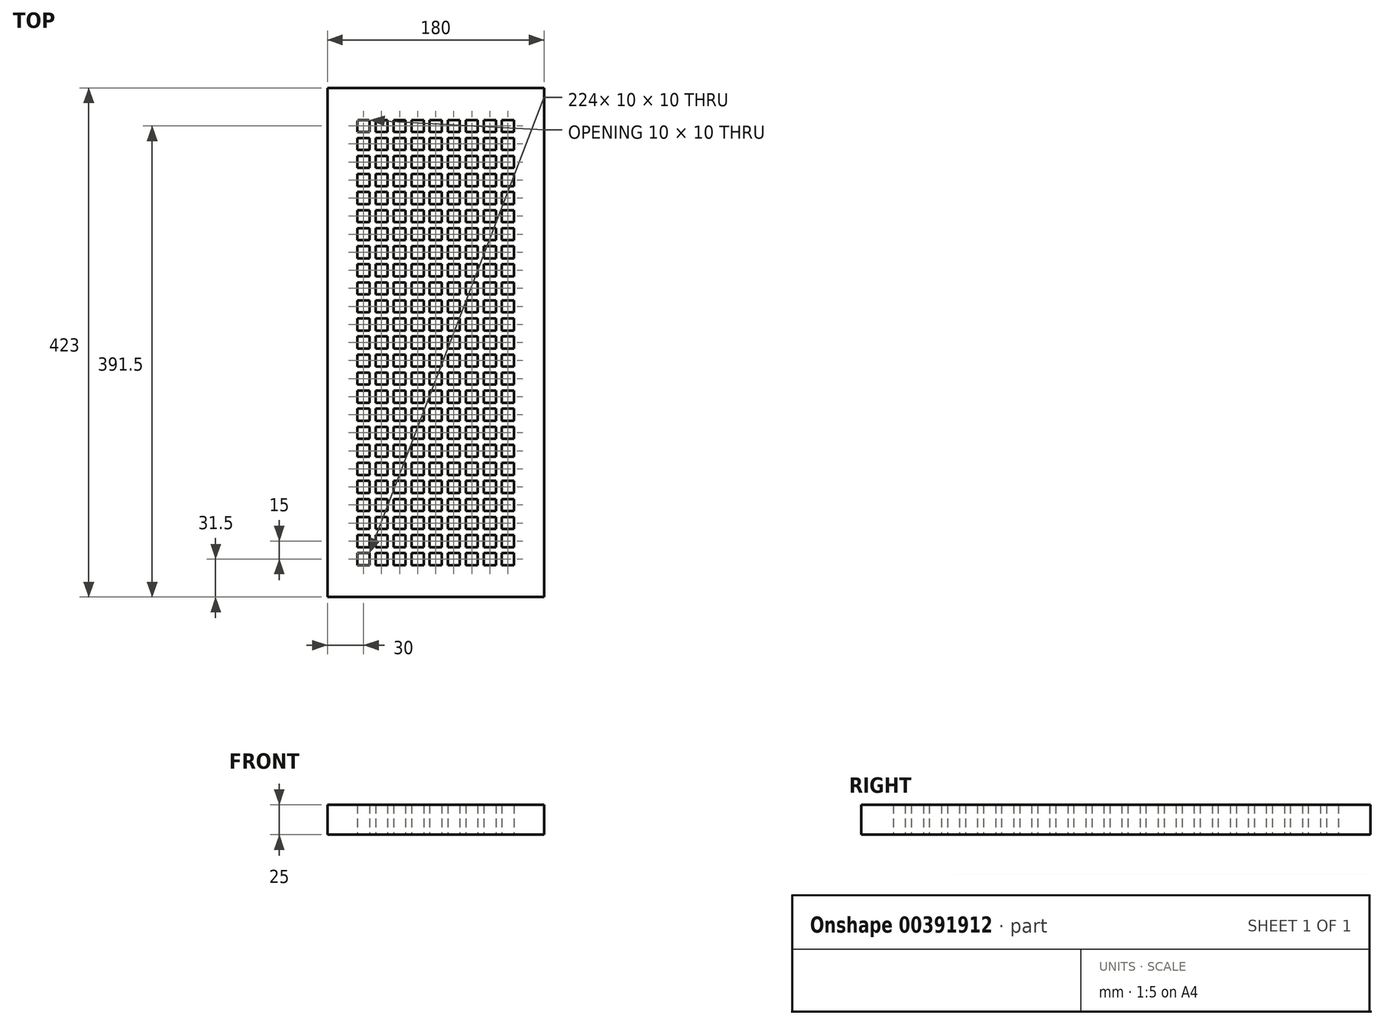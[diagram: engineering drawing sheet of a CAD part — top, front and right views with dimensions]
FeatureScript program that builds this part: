
annotation { "Feature Type Name" : "Feature", "Feature Type Description" : "" }
export const myFeature = defineFeature(function(context is Context, id is Id, definition is map)
    precondition{}
    {
        {
            var Q0;
            Q0=qCreatedBy(makeId("Top.planeOp"),FACE);
            var sketch = newSketch(context, id + "F0", { "sketchPlane" : qUnion([Q0])});
            skLineSegment(sketch, "E0.bottom", {"start": v(-180, 423) * mm, "end": v(0, 423) * mm});
            skLineSegment(sketch, "E0.top", {"start": v(-180, 0) * mm, "end": v(0, 0) * mm});
            skLineSegment(sketch, "E0.left", {"start": v(-180, 423) * mm, "end": v(-180, 0) * mm});
            skLineSegment(sketch, "E0.right", {"start": v(0, 423) * mm, "end": v(0, 0) * mm});
            skLineSegment(sketch, "E1", {"start": v(-153.5, 396.5) * mm, "end": v(-146.5, 396.5) * mm});
            skLineSegment(sketch, "E2", {"start": v(-155, 386.5) * mm, "end": v(-145, 386.5) * mm});
            skLineSegment(sketch, "E3", {"start": v(-145, 386.5) * mm, "end": v(-145, 395) * mm});
            skLineSegment(sketch, "E4.trimOffspring", {"start": v(-155, 386.5) * mm, "end": v(-155, 395) * mm});
            skLineSegment(sketch, "E5.0.1.0", {"start": v(-155, 371.5) * mm, "end": v(-155, 381.5) * mm});
            skLineSegment(sketch, "E5.0.1.1", {"start": v(-145, 371.5) * mm, "end": v(-145, 381.5) * mm});
            skLineSegment(sketch, "E5.0.1.2", {"start": v(-155, 371.5) * mm, "end": v(-145, 371.5) * mm});
            skLineSegment(sketch, "E5.0.1.3", {"start": v(-155, 381.5) * mm, "end": v(-145, 381.5) * mm});
            skLineSegment(sketch, "E5.0.2.0", {"start": v(-155, 356.5) * mm, "end": v(-155, 366.5) * mm});
            skLineSegment(sketch, "E5.0.2.1", {"start": v(-145, 356.5) * mm, "end": v(-145, 366.5) * mm});
            skLineSegment(sketch, "E5.0.2.2", {"start": v(-155, 356.5) * mm, "end": v(-145, 356.5) * mm});
            skLineSegment(sketch, "E5.0.2.3", {"start": v(-155, 366.5) * mm, "end": v(-145, 366.5) * mm});
            skLineSegment(sketch, "E5.0.3.0", {"start": v(-155, 341.5) * mm, "end": v(-155, 351.5) * mm});
            skLineSegment(sketch, "E5.0.3.1", {"start": v(-145, 341.5) * mm, "end": v(-145, 351.5) * mm});
            skLineSegment(sketch, "E5.0.3.2", {"start": v(-155, 341.5) * mm, "end": v(-145, 341.5) * mm});
            skLineSegment(sketch, "E5.0.3.3", {"start": v(-155, 351.5) * mm, "end": v(-145, 351.5) * mm});
            skLineSegment(sketch, "E5.0.4.0", {"start": v(-155, 326.5) * mm, "end": v(-155, 336.5) * mm});
            skLineSegment(sketch, "E5.0.4.1", {"start": v(-145, 326.5) * mm, "end": v(-145, 336.5) * mm});
            skLineSegment(sketch, "E5.0.4.2", {"start": v(-155, 326.5) * mm, "end": v(-145, 326.5) * mm});
            skLineSegment(sketch, "E5.0.4.3", {"start": v(-155, 336.5) * mm, "end": v(-145, 336.5) * mm});
            skLineSegment(sketch, "E5.0.5.0", {"start": v(-155, 311.5) * mm, "end": v(-155, 321.5) * mm});
            skLineSegment(sketch, "E5.0.5.1", {"start": v(-145, 311.5) * mm, "end": v(-145, 321.5) * mm});
            skLineSegment(sketch, "E5.0.5.2", {"start": v(-155, 311.5) * mm, "end": v(-145, 311.5) * mm});
            skLineSegment(sketch, "E5.0.5.3", {"start": v(-155, 321.5) * mm, "end": v(-145, 321.5) * mm});
            skLineSegment(sketch, "E5.0.6.0", {"start": v(-155, 296.5) * mm, "end": v(-155, 306.5) * mm});
            skLineSegment(sketch, "E5.0.6.1", {"start": v(-145, 296.5) * mm, "end": v(-145, 306.5) * mm});
            skLineSegment(sketch, "E5.0.6.2", {"start": v(-155, 296.5) * mm, "end": v(-145, 296.5) * mm});
            skLineSegment(sketch, "E5.0.6.3", {"start": v(-155, 306.5) * mm, "end": v(-145, 306.5) * mm});
            skLineSegment(sketch, "E5.0.7.0", {"start": v(-155, 281.5) * mm, "end": v(-155, 291.5) * mm});
            skLineSegment(sketch, "E5.0.7.1", {"start": v(-145, 281.5) * mm, "end": v(-145, 291.5) * mm});
            skLineSegment(sketch, "E5.0.7.2", {"start": v(-155, 281.5) * mm, "end": v(-145, 281.5) * mm});
            skLineSegment(sketch, "E5.0.7.3", {"start": v(-155, 291.5) * mm, "end": v(-145, 291.5) * mm});
            skLineSegment(sketch, "E5.0.8.0", {"start": v(-155, 266.5) * mm, "end": v(-155, 276.5) * mm});
            skLineSegment(sketch, "E5.0.8.1", {"start": v(-145, 266.5) * mm, "end": v(-145, 276.5) * mm});
            skLineSegment(sketch, "E5.0.8.2", {"start": v(-155, 266.5) * mm, "end": v(-145, 266.5) * mm});
            skLineSegment(sketch, "E5.0.8.3", {"start": v(-155, 276.5) * mm, "end": v(-145, 276.5) * mm});
            skLineSegment(sketch, "E5.0.9.0", {"start": v(-155, 251.5) * mm, "end": v(-155, 261.5) * mm});
            skLineSegment(sketch, "E5.0.9.1", {"start": v(-145, 251.5) * mm, "end": v(-145, 261.5) * mm});
            skLineSegment(sketch, "E5.0.9.2", {"start": v(-155, 251.5) * mm, "end": v(-145, 251.5) * mm});
            skLineSegment(sketch, "E5.0.9.3", {"start": v(-155, 261.5) * mm, "end": v(-145, 261.5) * mm});
            skLineSegment(sketch, "E5.0.10.0", {"start": v(-155, 236.5) * mm, "end": v(-155, 246.5) * mm});
            skLineSegment(sketch, "E5.0.10.1", {"start": v(-145, 236.5) * mm, "end": v(-145, 246.5) * mm});
            skLineSegment(sketch, "E5.0.10.2", {"start": v(-155, 236.5) * mm, "end": v(-145, 236.5) * mm});
            skLineSegment(sketch, "E5.0.10.3", {"start": v(-155, 246.5) * mm, "end": v(-145, 246.5) * mm});
            skLineSegment(sketch, "E5.0.11.0", {"start": v(-155, 221.5) * mm, "end": v(-155, 231.5) * mm});
            skLineSegment(sketch, "E5.0.11.1", {"start": v(-145, 221.5) * mm, "end": v(-145, 231.5) * mm});
            skLineSegment(sketch, "E5.0.11.2", {"start": v(-155, 221.5) * mm, "end": v(-145, 221.5) * mm});
            skLineSegment(sketch, "E5.0.11.3", {"start": v(-155, 231.5) * mm, "end": v(-145, 231.5) * mm});
            skLineSegment(sketch, "E5.0.12.0", {"start": v(-155, 206.5) * mm, "end": v(-155, 216.5) * mm});
            skLineSegment(sketch, "E5.0.12.1", {"start": v(-145, 206.5) * mm, "end": v(-145, 216.5) * mm});
            skLineSegment(sketch, "E5.0.12.2", {"start": v(-155, 206.5) * mm, "end": v(-145, 206.5) * mm});
            skLineSegment(sketch, "E5.0.12.3", {"start": v(-155, 216.5) * mm, "end": v(-145, 216.5) * mm});
            skLineSegment(sketch, "E5.0.13.0", {"start": v(-155, 191.5) * mm, "end": v(-155, 201.5) * mm});
            skLineSegment(sketch, "E5.0.13.1", {"start": v(-145, 191.5) * mm, "end": v(-145, 201.5) * mm});
            skLineSegment(sketch, "E5.0.13.2", {"start": v(-155, 191.5) * mm, "end": v(-145, 191.5) * mm});
            skLineSegment(sketch, "E5.0.13.3", {"start": v(-155, 201.5) * mm, "end": v(-145, 201.5) * mm});
            skLineSegment(sketch, "E5.0.14.0", {"start": v(-155, 176.5) * mm, "end": v(-155, 186.5) * mm});
            skLineSegment(sketch, "E5.0.14.1", {"start": v(-145, 176.5) * mm, "end": v(-145, 186.5) * mm});
            skLineSegment(sketch, "E5.0.14.2", {"start": v(-155, 176.5) * mm, "end": v(-145, 176.5) * mm});
            skLineSegment(sketch, "E5.0.14.3", {"start": v(-155, 186.5) * mm, "end": v(-145, 186.5) * mm});
            skLineSegment(sketch, "E5.0.15.0", {"start": v(-155, 161.5) * mm, "end": v(-155, 171.5) * mm});
            skLineSegment(sketch, "E5.0.15.1", {"start": v(-145, 161.5) * mm, "end": v(-145, 171.5) * mm});
            skLineSegment(sketch, "E5.0.15.2", {"start": v(-155, 161.5) * mm, "end": v(-145, 161.5) * mm});
            skLineSegment(sketch, "E5.0.15.3", {"start": v(-155, 171.5) * mm, "end": v(-145, 171.5) * mm});
            skLineSegment(sketch, "E5.0.16.0", {"start": v(-155, 146.5) * mm, "end": v(-155, 156.5) * mm});
            skLineSegment(sketch, "E5.0.16.1", {"start": v(-145, 146.5) * mm, "end": v(-145, 156.5) * mm});
            skLineSegment(sketch, "E5.0.16.2", {"start": v(-155, 146.5) * mm, "end": v(-145, 146.5) * mm});
            skLineSegment(sketch, "E5.0.16.3", {"start": v(-155, 156.5) * mm, "end": v(-145, 156.5) * mm});
            skLineSegment(sketch, "E5.0.17.0", {"start": v(-155, 131.5) * mm, "end": v(-155, 141.5) * mm});
            skLineSegment(sketch, "E5.0.17.1", {"start": v(-145, 131.5) * mm, "end": v(-145, 141.5) * mm});
            skLineSegment(sketch, "E5.0.17.2", {"start": v(-155, 131.5) * mm, "end": v(-145, 131.5) * mm});
            skLineSegment(sketch, "E5.0.17.3", {"start": v(-155, 141.5) * mm, "end": v(-145, 141.5) * mm});
            skLineSegment(sketch, "E5.0.18.0", {"start": v(-155, 116.5) * mm, "end": v(-155, 126.5) * mm});
            skLineSegment(sketch, "E5.0.18.1", {"start": v(-145, 116.5) * mm, "end": v(-145, 126.5) * mm});
            skLineSegment(sketch, "E5.0.18.2", {"start": v(-155, 116.5) * mm, "end": v(-145, 116.5) * mm});
            skLineSegment(sketch, "E5.0.18.3", {"start": v(-155, 126.5) * mm, "end": v(-145, 126.5) * mm});
            skLineSegment(sketch, "E5.0.19.0", {"start": v(-155, 101.5) * mm, "end": v(-155, 111.5) * mm});
            skLineSegment(sketch, "E5.0.19.1", {"start": v(-145, 101.5) * mm, "end": v(-145, 111.5) * mm});
            skLineSegment(sketch, "E5.0.19.2", {"start": v(-155, 101.5) * mm, "end": v(-145, 101.5) * mm});
            skLineSegment(sketch, "E5.0.19.3", {"start": v(-155, 111.5) * mm, "end": v(-145, 111.5) * mm});
            skLineSegment(sketch, "E5.0.20.0", {"start": v(-155, 86.5) * mm, "end": v(-155, 96.5) * mm});
            skLineSegment(sketch, "E5.0.20.1", {"start": v(-145, 86.5) * mm, "end": v(-145, 96.5) * mm});
            skLineSegment(sketch, "E5.0.20.2", {"start": v(-155, 86.5) * mm, "end": v(-145, 86.5) * mm});
            skLineSegment(sketch, "E5.0.20.3", {"start": v(-155, 96.5) * mm, "end": v(-145, 96.5) * mm});
            skLineSegment(sketch, "E5.0.21.0", {"start": v(-155, 71.5) * mm, "end": v(-155, 81.5) * mm});
            skLineSegment(sketch, "E5.0.21.1", {"start": v(-145, 71.5) * mm, "end": v(-145, 81.5) * mm});
            skLineSegment(sketch, "E5.0.21.2", {"start": v(-155, 71.5) * mm, "end": v(-145, 71.5) * mm});
            skLineSegment(sketch, "E5.0.21.3", {"start": v(-155, 81.5) * mm, "end": v(-145, 81.5) * mm});
            skLineSegment(sketch, "E5.0.22.0", {"start": v(-155, 56.5) * mm, "end": v(-155, 66.5) * mm});
            skLineSegment(sketch, "E5.0.22.1", {"start": v(-145, 56.5) * mm, "end": v(-145, 66.5) * mm});
            skLineSegment(sketch, "E5.0.22.2", {"start": v(-155, 56.5) * mm, "end": v(-145, 56.5) * mm});
            skLineSegment(sketch, "E5.0.22.3", {"start": v(-155, 66.5) * mm, "end": v(-145, 66.5) * mm});
            skLineSegment(sketch, "E5.0.23.0", {"start": v(-155, 41.5) * mm, "end": v(-155, 51.5) * mm});
            skLineSegment(sketch, "E5.0.23.1", {"start": v(-145, 41.5) * mm, "end": v(-145, 51.5) * mm});
            skLineSegment(sketch, "E5.0.23.2", {"start": v(-155, 41.5) * mm, "end": v(-145, 41.5) * mm});
            skLineSegment(sketch, "E5.0.23.3", {"start": v(-155, 51.5) * mm, "end": v(-145, 51.5) * mm});
            skLineSegment(sketch, "E5.0.24.0", {"start": v(-155, 26.5) * mm, "end": v(-155, 36.5) * mm});
            skLineSegment(sketch, "E5.0.24.1", {"start": v(-145, 26.5) * mm, "end": v(-145, 36.5) * mm});
            skLineSegment(sketch, "E5.0.24.2", {"start": v(-155, 26.5) * mm, "end": v(-145, 26.5) * mm});
            skLineSegment(sketch, "E5.0.24.3", {"start": v(-155, 36.5) * mm, "end": v(-145, 36.5) * mm});
            skLineSegment(sketch, "E5.1.0.0", {"start": v(-140, 386.5) * mm, "end": v(-140, 396.5) * mm});
            skLineSegment(sketch, "E5.1.0.1", {"start": v(-130, 386.5) * mm, "end": v(-130, 396.5) * mm});
            skLineSegment(sketch, "E5.1.0.2", {"start": v(-140, 386.5) * mm, "end": v(-130, 386.5) * mm});
            skLineSegment(sketch, "E5.1.0.3", {"start": v(-140, 396.5) * mm, "end": v(-130, 396.5) * mm});
            skLineSegment(sketch, "E5.1.1.0", {"start": v(-140, 371.5) * mm, "end": v(-140, 381.5) * mm});
            skLineSegment(sketch, "E5.1.1.1", {"start": v(-130, 371.5) * mm, "end": v(-130, 381.5) * mm});
            skLineSegment(sketch, "E5.1.1.2", {"start": v(-140, 371.5) * mm, "end": v(-130, 371.5) * mm});
            skLineSegment(sketch, "E5.1.1.3", {"start": v(-140, 381.5) * mm, "end": v(-130, 381.5) * mm});
            skLineSegment(sketch, "E5.1.2.0", {"start": v(-140, 356.5) * mm, "end": v(-140, 366.5) * mm});
            skLineSegment(sketch, "E5.1.2.1", {"start": v(-130, 356.5) * mm, "end": v(-130, 366.5) * mm});
            skLineSegment(sketch, "E5.1.2.2", {"start": v(-140, 356.5) * mm, "end": v(-130, 356.5) * mm});
            skLineSegment(sketch, "E5.1.2.3", {"start": v(-140, 366.5) * mm, "end": v(-130, 366.5) * mm});
            skLineSegment(sketch, "E5.1.3.0", {"start": v(-140, 341.5) * mm, "end": v(-140, 351.5) * mm});
            skLineSegment(sketch, "E5.1.3.1", {"start": v(-130, 341.5) * mm, "end": v(-130, 351.5) * mm});
            skLineSegment(sketch, "E5.1.3.2", {"start": v(-140, 341.5) * mm, "end": v(-130, 341.5) * mm});
            skLineSegment(sketch, "E5.1.3.3", {"start": v(-140, 351.5) * mm, "end": v(-130, 351.5) * mm});
            skLineSegment(sketch, "E5.1.4.0", {"start": v(-140, 326.5) * mm, "end": v(-140, 336.5) * mm});
            skLineSegment(sketch, "E5.1.4.1", {"start": v(-130, 326.5) * mm, "end": v(-130, 336.5) * mm});
            skLineSegment(sketch, "E5.1.4.2", {"start": v(-140, 326.5) * mm, "end": v(-130, 326.5) * mm});
            skLineSegment(sketch, "E5.1.4.3", {"start": v(-140, 336.5) * mm, "end": v(-130, 336.5) * mm});
            skLineSegment(sketch, "E5.1.5.0", {"start": v(-140, 311.5) * mm, "end": v(-140, 321.5) * mm});
            skLineSegment(sketch, "E5.1.5.1", {"start": v(-130, 311.5) * mm, "end": v(-130, 321.5) * mm});
            skLineSegment(sketch, "E5.1.5.2", {"start": v(-140, 311.5) * mm, "end": v(-130, 311.5) * mm});
            skLineSegment(sketch, "E5.1.5.3", {"start": v(-140, 321.5) * mm, "end": v(-130, 321.5) * mm});
            skLineSegment(sketch, "E5.1.6.0", {"start": v(-140, 296.5) * mm, "end": v(-140, 306.5) * mm});
            skLineSegment(sketch, "E5.1.6.1", {"start": v(-130, 296.5) * mm, "end": v(-130, 306.5) * mm});
            skLineSegment(sketch, "E5.1.6.2", {"start": v(-140, 296.5) * mm, "end": v(-130, 296.5) * mm});
            skLineSegment(sketch, "E5.1.6.3", {"start": v(-140, 306.5) * mm, "end": v(-130, 306.5) * mm});
            skLineSegment(sketch, "E5.1.7.0", {"start": v(-140, 281.5) * mm, "end": v(-140, 291.5) * mm});
            skLineSegment(sketch, "E5.1.7.1", {"start": v(-130, 281.5) * mm, "end": v(-130, 291.5) * mm});
            skLineSegment(sketch, "E5.1.7.2", {"start": v(-140, 281.5) * mm, "end": v(-130, 281.5) * mm});
            skLineSegment(sketch, "E5.1.7.3", {"start": v(-140, 291.5) * mm, "end": v(-130, 291.5) * mm});
            skLineSegment(sketch, "E5.1.8.0", {"start": v(-140, 266.5) * mm, "end": v(-140, 276.5) * mm});
            skLineSegment(sketch, "E5.1.8.1", {"start": v(-130, 266.5) * mm, "end": v(-130, 276.5) * mm});
            skLineSegment(sketch, "E5.1.8.2", {"start": v(-140, 266.5) * mm, "end": v(-130, 266.5) * mm});
            skLineSegment(sketch, "E5.1.8.3", {"start": v(-140, 276.5) * mm, "end": v(-130, 276.5) * mm});
            skLineSegment(sketch, "E5.1.9.0", {"start": v(-140, 251.5) * mm, "end": v(-140, 261.5) * mm});
            skLineSegment(sketch, "E5.1.9.1", {"start": v(-130, 251.5) * mm, "end": v(-130, 261.5) * mm});
            skLineSegment(sketch, "E5.1.9.2", {"start": v(-140, 251.5) * mm, "end": v(-130, 251.5) * mm});
            skLineSegment(sketch, "E5.1.9.3", {"start": v(-140, 261.5) * mm, "end": v(-130, 261.5) * mm});
            skLineSegment(sketch, "E5.1.10.0", {"start": v(-140, 236.5) * mm, "end": v(-140, 246.5) * mm});
            skLineSegment(sketch, "E5.1.10.1", {"start": v(-130, 236.5) * mm, "end": v(-130, 246.5) * mm});
            skLineSegment(sketch, "E5.1.10.2", {"start": v(-140, 236.5) * mm, "end": v(-130, 236.5) * mm});
            skLineSegment(sketch, "E5.1.10.3", {"start": v(-140, 246.5) * mm, "end": v(-130, 246.5) * mm});
            skLineSegment(sketch, "E5.1.11.0", {"start": v(-140, 221.5) * mm, "end": v(-140, 231.5) * mm});
            skLineSegment(sketch, "E5.1.11.1", {"start": v(-130, 221.5) * mm, "end": v(-130, 231.5) * mm});
            skLineSegment(sketch, "E5.1.11.2", {"start": v(-140, 221.5) * mm, "end": v(-130, 221.5) * mm});
            skLineSegment(sketch, "E5.1.11.3", {"start": v(-140, 231.5) * mm, "end": v(-130, 231.5) * mm});
            skLineSegment(sketch, "E5.1.12.0", {"start": v(-140, 206.5) * mm, "end": v(-140, 216.5) * mm});
            skLineSegment(sketch, "E5.1.12.1", {"start": v(-130, 206.5) * mm, "end": v(-130, 216.5) * mm});
            skLineSegment(sketch, "E5.1.12.2", {"start": v(-140, 206.5) * mm, "end": v(-130, 206.5) * mm});
            skLineSegment(sketch, "E5.1.12.3", {"start": v(-140, 216.5) * mm, "end": v(-130, 216.5) * mm});
            skLineSegment(sketch, "E5.1.13.0", {"start": v(-140, 191.5) * mm, "end": v(-140, 201.5) * mm});
            skLineSegment(sketch, "E5.1.13.1", {"start": v(-130, 191.5) * mm, "end": v(-130, 201.5) * mm});
            skLineSegment(sketch, "E5.1.13.2", {"start": v(-140, 191.5) * mm, "end": v(-130, 191.5) * mm});
            skLineSegment(sketch, "E5.1.13.3", {"start": v(-140, 201.5) * mm, "end": v(-130, 201.5) * mm});
            skLineSegment(sketch, "E5.1.14.0", {"start": v(-140, 176.5) * mm, "end": v(-140, 186.5) * mm});
            skLineSegment(sketch, "E5.1.14.1", {"start": v(-130, 176.5) * mm, "end": v(-130, 186.5) * mm});
            skLineSegment(sketch, "E5.1.14.2", {"start": v(-140, 176.5) * mm, "end": v(-130, 176.5) * mm});
            skLineSegment(sketch, "E5.1.14.3", {"start": v(-140, 186.5) * mm, "end": v(-130, 186.5) * mm});
            skLineSegment(sketch, "E5.1.15.0", {"start": v(-140, 161.5) * mm, "end": v(-140, 171.5) * mm});
            skLineSegment(sketch, "E5.1.15.1", {"start": v(-130, 161.5) * mm, "end": v(-130, 171.5) * mm});
            skLineSegment(sketch, "E5.1.15.2", {"start": v(-140, 161.5) * mm, "end": v(-130, 161.5) * mm});
            skLineSegment(sketch, "E5.1.15.3", {"start": v(-140, 171.5) * mm, "end": v(-130, 171.5) * mm});
            skLineSegment(sketch, "E5.1.16.0", {"start": v(-140, 146.5) * mm, "end": v(-140, 156.5) * mm});
            skLineSegment(sketch, "E5.1.16.1", {"start": v(-130, 146.5) * mm, "end": v(-130, 156.5) * mm});
            skLineSegment(sketch, "E5.1.16.2", {"start": v(-140, 146.5) * mm, "end": v(-130, 146.5) * mm});
            skLineSegment(sketch, "E5.1.16.3", {"start": v(-140, 156.5) * mm, "end": v(-130, 156.5) * mm});
            skLineSegment(sketch, "E5.1.17.0", {"start": v(-140, 131.5) * mm, "end": v(-140, 141.5) * mm});
            skLineSegment(sketch, "E5.1.17.1", {"start": v(-130, 131.5) * mm, "end": v(-130, 141.5) * mm});
            skLineSegment(sketch, "E5.1.17.2", {"start": v(-140, 131.5) * mm, "end": v(-130, 131.5) * mm});
            skLineSegment(sketch, "E5.1.17.3", {"start": v(-140, 141.5) * mm, "end": v(-130, 141.5) * mm});
            skLineSegment(sketch, "E5.1.18.0", {"start": v(-140, 116.5) * mm, "end": v(-140, 126.5) * mm});
            skLineSegment(sketch, "E5.1.18.1", {"start": v(-130, 116.5) * mm, "end": v(-130, 126.5) * mm});
            skLineSegment(sketch, "E5.1.18.2", {"start": v(-140, 116.5) * mm, "end": v(-130, 116.5) * mm});
            skLineSegment(sketch, "E5.1.18.3", {"start": v(-140, 126.5) * mm, "end": v(-130, 126.5) * mm});
            skLineSegment(sketch, "E5.1.19.0", {"start": v(-140, 101.5) * mm, "end": v(-140, 111.5) * mm});
            skLineSegment(sketch, "E5.1.19.1", {"start": v(-130, 101.5) * mm, "end": v(-130, 111.5) * mm});
            skLineSegment(sketch, "E5.1.19.2", {"start": v(-140, 101.5) * mm, "end": v(-130, 101.5) * mm});
            skLineSegment(sketch, "E5.1.19.3", {"start": v(-140, 111.5) * mm, "end": v(-130, 111.5) * mm});
            skLineSegment(sketch, "E5.1.20.0", {"start": v(-140, 86.5) * mm, "end": v(-140, 96.5) * mm});
            skLineSegment(sketch, "E5.1.20.1", {"start": v(-130, 86.5) * mm, "end": v(-130, 96.5) * mm});
            skLineSegment(sketch, "E5.1.20.2", {"start": v(-140, 86.5) * mm, "end": v(-130, 86.5) * mm});
            skLineSegment(sketch, "E5.1.20.3", {"start": v(-140, 96.5) * mm, "end": v(-130, 96.5) * mm});
            skLineSegment(sketch, "E5.1.21.0", {"start": v(-140, 71.5) * mm, "end": v(-140, 81.5) * mm});
            skLineSegment(sketch, "E5.1.21.1", {"start": v(-130, 71.5) * mm, "end": v(-130, 81.5) * mm});
            skLineSegment(sketch, "E5.1.21.2", {"start": v(-140, 71.5) * mm, "end": v(-130, 71.5) * mm});
            skLineSegment(sketch, "E5.1.21.3", {"start": v(-140, 81.5) * mm, "end": v(-130, 81.5) * mm});
            skLineSegment(sketch, "E5.1.22.0", {"start": v(-140, 56.5) * mm, "end": v(-140, 66.5) * mm});
            skLineSegment(sketch, "E5.1.22.1", {"start": v(-130, 56.5) * mm, "end": v(-130, 66.5) * mm});
            skLineSegment(sketch, "E5.1.22.2", {"start": v(-140, 56.5) * mm, "end": v(-130, 56.5) * mm});
            skLineSegment(sketch, "E5.1.22.3", {"start": v(-140, 66.5) * mm, "end": v(-130, 66.5) * mm});
            skLineSegment(sketch, "E5.1.23.0", {"start": v(-140, 41.5) * mm, "end": v(-140, 51.5) * mm});
            skLineSegment(sketch, "E5.1.23.1", {"start": v(-130, 41.5) * mm, "end": v(-130, 51.5) * mm});
            skLineSegment(sketch, "E5.1.23.2", {"start": v(-140, 41.5) * mm, "end": v(-130, 41.5) * mm});
            skLineSegment(sketch, "E5.1.23.3", {"start": v(-140, 51.5) * mm, "end": v(-130, 51.5) * mm});
            skLineSegment(sketch, "E5.1.24.0", {"start": v(-140, 26.5) * mm, "end": v(-140, 36.5) * mm});
            skLineSegment(sketch, "E5.1.24.1", {"start": v(-130, 26.5) * mm, "end": v(-130, 36.5) * mm});
            skLineSegment(sketch, "E5.1.24.2", {"start": v(-140, 26.5) * mm, "end": v(-130, 26.5) * mm});
            skLineSegment(sketch, "E5.1.24.3", {"start": v(-140, 36.5) * mm, "end": v(-130, 36.5) * mm});
            skLineSegment(sketch, "E5.2.0.0", {"start": v(-125, 386.5) * mm, "end": v(-125, 396.5) * mm});
            skLineSegment(sketch, "E5.2.0.1", {"start": v(-115, 386.5) * mm, "end": v(-115, 396.5) * mm});
            skLineSegment(sketch, "E5.2.0.2", {"start": v(-125, 386.5) * mm, "end": v(-115, 386.5) * mm});
            skLineSegment(sketch, "E5.2.0.3", {"start": v(-125, 396.5) * mm, "end": v(-115, 396.5) * mm});
            skLineSegment(sketch, "E5.2.1.0", {"start": v(-125, 371.5) * mm, "end": v(-125, 381.5) * mm});
            skLineSegment(sketch, "E5.2.1.1", {"start": v(-115, 371.5) * mm, "end": v(-115, 381.5) * mm});
            skLineSegment(sketch, "E5.2.1.2", {"start": v(-125, 371.5) * mm, "end": v(-115, 371.5) * mm});
            skLineSegment(sketch, "E5.2.1.3", {"start": v(-125, 381.5) * mm, "end": v(-115, 381.5) * mm});
            skLineSegment(sketch, "E5.2.2.0", {"start": v(-125, 356.5) * mm, "end": v(-125, 366.5) * mm});
            skLineSegment(sketch, "E5.2.2.1", {"start": v(-115, 356.5) * mm, "end": v(-115, 366.5) * mm});
            skLineSegment(sketch, "E5.2.2.2", {"start": v(-125, 356.5) * mm, "end": v(-115, 356.5) * mm});
            skLineSegment(sketch, "E5.2.2.3", {"start": v(-125, 366.5) * mm, "end": v(-115, 366.5) * mm});
            skLineSegment(sketch, "E5.2.3.0", {"start": v(-125, 341.5) * mm, "end": v(-125, 351.5) * mm});
            skLineSegment(sketch, "E5.2.3.1", {"start": v(-115, 341.5) * mm, "end": v(-115, 351.5) * mm});
            skLineSegment(sketch, "E5.2.3.2", {"start": v(-125, 341.5) * mm, "end": v(-115, 341.5) * mm});
            skLineSegment(sketch, "E5.2.3.3", {"start": v(-125, 351.5) * mm, "end": v(-115, 351.5) * mm});
            skLineSegment(sketch, "E5.2.4.0", {"start": v(-125, 326.5) * mm, "end": v(-125, 336.5) * mm});
            skLineSegment(sketch, "E5.2.4.1", {"start": v(-115, 326.5) * mm, "end": v(-115, 336.5) * mm});
            skLineSegment(sketch, "E5.2.4.2", {"start": v(-125, 326.5) * mm, "end": v(-115, 326.5) * mm});
            skLineSegment(sketch, "E5.2.4.3", {"start": v(-125, 336.5) * mm, "end": v(-115, 336.5) * mm});
            skLineSegment(sketch, "E5.2.5.0", {"start": v(-125, 311.5) * mm, "end": v(-125, 321.5) * mm});
            skLineSegment(sketch, "E5.2.5.1", {"start": v(-115, 311.5) * mm, "end": v(-115, 321.5) * mm});
            skLineSegment(sketch, "E5.2.5.2", {"start": v(-125, 311.5) * mm, "end": v(-115, 311.5) * mm});
            skLineSegment(sketch, "E5.2.5.3", {"start": v(-125, 321.5) * mm, "end": v(-115, 321.5) * mm});
            skLineSegment(sketch, "E5.2.6.0", {"start": v(-125, 296.5) * mm, "end": v(-125, 306.5) * mm});
            skLineSegment(sketch, "E5.2.6.1", {"start": v(-115, 296.5) * mm, "end": v(-115, 306.5) * mm});
            skLineSegment(sketch, "E5.2.6.2", {"start": v(-125, 296.5) * mm, "end": v(-115, 296.5) * mm});
            skLineSegment(sketch, "E5.2.6.3", {"start": v(-125, 306.5) * mm, "end": v(-115, 306.5) * mm});
            skLineSegment(sketch, "E5.2.7.0", {"start": v(-125, 281.5) * mm, "end": v(-125, 291.5) * mm});
            skLineSegment(sketch, "E5.2.7.1", {"start": v(-115, 281.5) * mm, "end": v(-115, 291.5) * mm});
            skLineSegment(sketch, "E5.2.7.2", {"start": v(-125, 281.5) * mm, "end": v(-115, 281.5) * mm});
            skLineSegment(sketch, "E5.2.7.3", {"start": v(-125, 291.5) * mm, "end": v(-115, 291.5) * mm});
            skLineSegment(sketch, "E5.2.8.0", {"start": v(-125, 266.5) * mm, "end": v(-125, 276.5) * mm});
            skLineSegment(sketch, "E5.2.8.1", {"start": v(-115, 266.5) * mm, "end": v(-115, 276.5) * mm});
            skLineSegment(sketch, "E5.2.8.2", {"start": v(-125, 266.5) * mm, "end": v(-115, 266.5) * mm});
            skLineSegment(sketch, "E5.2.8.3", {"start": v(-125, 276.5) * mm, "end": v(-115, 276.5) * mm});
            skLineSegment(sketch, "E5.2.9.0", {"start": v(-125, 251.5) * mm, "end": v(-125, 261.5) * mm});
            skLineSegment(sketch, "E5.2.9.1", {"start": v(-115, 251.5) * mm, "end": v(-115, 261.5) * mm});
            skLineSegment(sketch, "E5.2.9.2", {"start": v(-125, 251.5) * mm, "end": v(-115, 251.5) * mm});
            skLineSegment(sketch, "E5.2.9.3", {"start": v(-125, 261.5) * mm, "end": v(-115, 261.5) * mm});
            skLineSegment(sketch, "E5.2.10.0", {"start": v(-125, 236.5) * mm, "end": v(-125, 246.5) * mm});
            skLineSegment(sketch, "E5.2.10.1", {"start": v(-115, 236.5) * mm, "end": v(-115, 246.5) * mm});
            skLineSegment(sketch, "E5.2.10.2", {"start": v(-125, 236.5) * mm, "end": v(-115, 236.5) * mm});
            skLineSegment(sketch, "E5.2.10.3", {"start": v(-125, 246.5) * mm, "end": v(-115, 246.5) * mm});
            skLineSegment(sketch, "E5.2.11.0", {"start": v(-125, 221.5) * mm, "end": v(-125, 231.5) * mm});
            skLineSegment(sketch, "E5.2.11.1", {"start": v(-115, 221.5) * mm, "end": v(-115, 231.5) * mm});
            skLineSegment(sketch, "E5.2.11.2", {"start": v(-125, 221.5) * mm, "end": v(-115, 221.5) * mm});
            skLineSegment(sketch, "E5.2.11.3", {"start": v(-125, 231.5) * mm, "end": v(-115, 231.5) * mm});
            skLineSegment(sketch, "E5.2.12.0", {"start": v(-125, 206.5) * mm, "end": v(-125, 216.5) * mm});
            skLineSegment(sketch, "E5.2.12.1", {"start": v(-115, 206.5) * mm, "end": v(-115, 216.5) * mm});
            skLineSegment(sketch, "E5.2.12.2", {"start": v(-125, 206.5) * mm, "end": v(-115, 206.5) * mm});
            skLineSegment(sketch, "E5.2.12.3", {"start": v(-125, 216.5) * mm, "end": v(-115, 216.5) * mm});
            skLineSegment(sketch, "E5.2.13.0", {"start": v(-125, 191.5) * mm, "end": v(-125, 201.5) * mm});
            skLineSegment(sketch, "E5.2.13.1", {"start": v(-115, 191.5) * mm, "end": v(-115, 201.5) * mm});
            skLineSegment(sketch, "E5.2.13.2", {"start": v(-125, 191.5) * mm, "end": v(-115, 191.5) * mm});
            skLineSegment(sketch, "E5.2.13.3", {"start": v(-125, 201.5) * mm, "end": v(-115, 201.5) * mm});
            skLineSegment(sketch, "E5.2.14.0", {"start": v(-125, 176.5) * mm, "end": v(-125, 186.5) * mm});
            skLineSegment(sketch, "E5.2.14.1", {"start": v(-115, 176.5) * mm, "end": v(-115, 186.5) * mm});
            skLineSegment(sketch, "E5.2.14.2", {"start": v(-125, 176.5) * mm, "end": v(-115, 176.5) * mm});
            skLineSegment(sketch, "E5.2.14.3", {"start": v(-125, 186.5) * mm, "end": v(-115, 186.5) * mm});
            skLineSegment(sketch, "E5.2.15.0", {"start": v(-125, 161.5) * mm, "end": v(-125, 171.5) * mm});
            skLineSegment(sketch, "E5.2.15.1", {"start": v(-115, 161.5) * mm, "end": v(-115, 171.5) * mm});
            skLineSegment(sketch, "E5.2.15.2", {"start": v(-125, 161.5) * mm, "end": v(-115, 161.5) * mm});
            skLineSegment(sketch, "E5.2.15.3", {"start": v(-125, 171.5) * mm, "end": v(-115, 171.5) * mm});
            skLineSegment(sketch, "E5.2.16.0", {"start": v(-125, 146.5) * mm, "end": v(-125, 156.5) * mm});
            skLineSegment(sketch, "E5.2.16.1", {"start": v(-115, 146.5) * mm, "end": v(-115, 156.5) * mm});
            skLineSegment(sketch, "E5.2.16.2", {"start": v(-125, 146.5) * mm, "end": v(-115, 146.5) * mm});
            skLineSegment(sketch, "E5.2.16.3", {"start": v(-125, 156.5) * mm, "end": v(-115, 156.5) * mm});
            skLineSegment(sketch, "E5.2.17.0", {"start": v(-125, 131.5) * mm, "end": v(-125, 141.5) * mm});
            skLineSegment(sketch, "E5.2.17.1", {"start": v(-115, 131.5) * mm, "end": v(-115, 141.5) * mm});
            skLineSegment(sketch, "E5.2.17.2", {"start": v(-125, 131.5) * mm, "end": v(-115, 131.5) * mm});
            skLineSegment(sketch, "E5.2.17.3", {"start": v(-125, 141.5) * mm, "end": v(-115, 141.5) * mm});
            skLineSegment(sketch, "E5.2.18.0", {"start": v(-125, 116.5) * mm, "end": v(-125, 126.5) * mm});
            skLineSegment(sketch, "E5.2.18.1", {"start": v(-115, 116.5) * mm, "end": v(-115, 126.5) * mm});
            skLineSegment(sketch, "E5.2.18.2", {"start": v(-125, 116.5) * mm, "end": v(-115, 116.5) * mm});
            skLineSegment(sketch, "E5.2.18.3", {"start": v(-125, 126.5) * mm, "end": v(-115, 126.5) * mm});
            skLineSegment(sketch, "E5.2.19.0", {"start": v(-125, 101.5) * mm, "end": v(-125, 111.5) * mm});
            skLineSegment(sketch, "E5.2.19.1", {"start": v(-115, 101.5) * mm, "end": v(-115, 111.5) * mm});
            skLineSegment(sketch, "E5.2.19.2", {"start": v(-125, 101.5) * mm, "end": v(-115, 101.5) * mm});
            skLineSegment(sketch, "E5.2.19.3", {"start": v(-125, 111.5) * mm, "end": v(-115, 111.5) * mm});
            skLineSegment(sketch, "E5.2.20.0", {"start": v(-125, 86.5) * mm, "end": v(-125, 96.5) * mm});
            skLineSegment(sketch, "E5.2.20.1", {"start": v(-115, 86.5) * mm, "end": v(-115, 96.5) * mm});
            skLineSegment(sketch, "E5.2.20.2", {"start": v(-125, 86.5) * mm, "end": v(-115, 86.5) * mm});
            skLineSegment(sketch, "E5.2.20.3", {"start": v(-125, 96.5) * mm, "end": v(-115, 96.5) * mm});
            skLineSegment(sketch, "E5.2.21.0", {"start": v(-125, 71.5) * mm, "end": v(-125, 81.5) * mm});
            skLineSegment(sketch, "E5.2.21.1", {"start": v(-115, 71.5) * mm, "end": v(-115, 81.5) * mm});
            skLineSegment(sketch, "E5.2.21.2", {"start": v(-125, 71.5) * mm, "end": v(-115, 71.5) * mm});
            skLineSegment(sketch, "E5.2.21.3", {"start": v(-125, 81.5) * mm, "end": v(-115, 81.5) * mm});
            skLineSegment(sketch, "E5.2.22.0", {"start": v(-125, 56.5) * mm, "end": v(-125, 66.5) * mm});
            skLineSegment(sketch, "E5.2.22.1", {"start": v(-115, 56.5) * mm, "end": v(-115, 66.5) * mm});
            skLineSegment(sketch, "E5.2.22.2", {"start": v(-125, 56.5) * mm, "end": v(-115, 56.5) * mm});
            skLineSegment(sketch, "E5.2.22.3", {"start": v(-125, 66.5) * mm, "end": v(-115, 66.5) * mm});
            skLineSegment(sketch, "E5.2.23.0", {"start": v(-125, 41.5) * mm, "end": v(-125, 51.5) * mm});
            skLineSegment(sketch, "E5.2.23.1", {"start": v(-115, 41.5) * mm, "end": v(-115, 51.5) * mm});
            skLineSegment(sketch, "E5.2.23.2", {"start": v(-125, 41.5) * mm, "end": v(-115, 41.5) * mm});
            skLineSegment(sketch, "E5.2.23.3", {"start": v(-125, 51.5) * mm, "end": v(-115, 51.5) * mm});
            skLineSegment(sketch, "E5.2.24.0", {"start": v(-125, 26.5) * mm, "end": v(-125, 36.5) * mm});
            skLineSegment(sketch, "E5.2.24.1", {"start": v(-115, 26.5) * mm, "end": v(-115, 36.5) * mm});
            skLineSegment(sketch, "E5.2.24.2", {"start": v(-125, 26.5) * mm, "end": v(-115, 26.5) * mm});
            skLineSegment(sketch, "E5.2.24.3", {"start": v(-125, 36.5) * mm, "end": v(-115, 36.5) * mm});
            skLineSegment(sketch, "E5.3.0.0", {"start": v(-110, 386.5) * mm, "end": v(-110, 396.5) * mm});
            skLineSegment(sketch, "E5.3.0.1", {"start": v(-100, 386.5) * mm, "end": v(-100, 396.5) * mm});
            skLineSegment(sketch, "E5.3.0.2", {"start": v(-110, 386.5) * mm, "end": v(-100, 386.5) * mm});
            skLineSegment(sketch, "E5.3.0.3", {"start": v(-110, 396.5) * mm, "end": v(-100, 396.5) * mm});
            skLineSegment(sketch, "E5.3.1.0", {"start": v(-110, 371.5) * mm, "end": v(-110, 381.5) * mm});
            skLineSegment(sketch, "E5.3.1.1", {"start": v(-100, 371.5) * mm, "end": v(-100, 381.5) * mm});
            skLineSegment(sketch, "E5.3.1.2", {"start": v(-110, 371.5) * mm, "end": v(-100, 371.5) * mm});
            skLineSegment(sketch, "E5.3.1.3", {"start": v(-110, 381.5) * mm, "end": v(-100, 381.5) * mm});
            skLineSegment(sketch, "E5.3.2.0", {"start": v(-110, 356.5) * mm, "end": v(-110, 366.5) * mm});
            skLineSegment(sketch, "E5.3.2.1", {"start": v(-100, 356.5) * mm, "end": v(-100, 366.5) * mm});
            skLineSegment(sketch, "E5.3.2.2", {"start": v(-110, 356.5) * mm, "end": v(-100, 356.5) * mm});
            skLineSegment(sketch, "E5.3.2.3", {"start": v(-110, 366.5) * mm, "end": v(-100, 366.5) * mm});
            skLineSegment(sketch, "E5.3.3.0", {"start": v(-110, 341.5) * mm, "end": v(-110, 351.5) * mm});
            skLineSegment(sketch, "E5.3.3.1", {"start": v(-100, 341.5) * mm, "end": v(-100, 351.5) * mm});
            skLineSegment(sketch, "E5.3.3.2", {"start": v(-110, 341.5) * mm, "end": v(-100, 341.5) * mm});
            skLineSegment(sketch, "E5.3.3.3", {"start": v(-110, 351.5) * mm, "end": v(-100, 351.5) * mm});
            skLineSegment(sketch, "E5.3.4.0", {"start": v(-110, 326.5) * mm, "end": v(-110, 336.5) * mm});
            skLineSegment(sketch, "E5.3.4.1", {"start": v(-100, 326.5) * mm, "end": v(-100, 336.5) * mm});
            skLineSegment(sketch, "E5.3.4.2", {"start": v(-110, 326.5) * mm, "end": v(-100, 326.5) * mm});
            skLineSegment(sketch, "E5.3.4.3", {"start": v(-110, 336.5) * mm, "end": v(-100, 336.5) * mm});
            skLineSegment(sketch, "E5.3.5.0", {"start": v(-110, 311.5) * mm, "end": v(-110, 321.5) * mm});
            skLineSegment(sketch, "E5.3.5.1", {"start": v(-100, 311.5) * mm, "end": v(-100, 321.5) * mm});
            skLineSegment(sketch, "E5.3.5.2", {"start": v(-110, 311.5) * mm, "end": v(-100, 311.5) * mm});
            skLineSegment(sketch, "E5.3.5.3", {"start": v(-110, 321.5) * mm, "end": v(-100, 321.5) * mm});
            skLineSegment(sketch, "E5.3.6.0", {"start": v(-110, 296.5) * mm, "end": v(-110, 306.5) * mm});
            skLineSegment(sketch, "E5.3.6.1", {"start": v(-100, 296.5) * mm, "end": v(-100, 306.5) * mm});
            skLineSegment(sketch, "E5.3.6.2", {"start": v(-110, 296.5) * mm, "end": v(-100, 296.5) * mm});
            skLineSegment(sketch, "E5.3.6.3", {"start": v(-110, 306.5) * mm, "end": v(-100, 306.5) * mm});
            skLineSegment(sketch, "E5.3.7.0", {"start": v(-110, 281.5) * mm, "end": v(-110, 291.5) * mm});
            skLineSegment(sketch, "E5.3.7.1", {"start": v(-100, 281.5) * mm, "end": v(-100, 291.5) * mm});
            skLineSegment(sketch, "E5.3.7.2", {"start": v(-110, 281.5) * mm, "end": v(-100, 281.5) * mm});
            skLineSegment(sketch, "E5.3.7.3", {"start": v(-110, 291.5) * mm, "end": v(-100, 291.5) * mm});
            skLineSegment(sketch, "E5.3.8.0", {"start": v(-110, 266.5) * mm, "end": v(-110, 276.5) * mm});
            skLineSegment(sketch, "E5.3.8.1", {"start": v(-100, 266.5) * mm, "end": v(-100, 276.5) * mm});
            skLineSegment(sketch, "E5.3.8.2", {"start": v(-110, 266.5) * mm, "end": v(-100, 266.5) * mm});
            skLineSegment(sketch, "E5.3.8.3", {"start": v(-110, 276.5) * mm, "end": v(-100, 276.5) * mm});
            skLineSegment(sketch, "E5.3.9.0", {"start": v(-110, 251.5) * mm, "end": v(-110, 261.5) * mm});
            skLineSegment(sketch, "E5.3.9.1", {"start": v(-100, 251.5) * mm, "end": v(-100, 261.5) * mm});
            skLineSegment(sketch, "E5.3.9.2", {"start": v(-110, 251.5) * mm, "end": v(-100, 251.5) * mm});
            skLineSegment(sketch, "E5.3.9.3", {"start": v(-110, 261.5) * mm, "end": v(-100, 261.5) * mm});
            skLineSegment(sketch, "E5.3.10.0", {"start": v(-110, 236.5) * mm, "end": v(-110, 246.5) * mm});
            skLineSegment(sketch, "E5.3.10.1", {"start": v(-100, 236.5) * mm, "end": v(-100, 246.5) * mm});
            skLineSegment(sketch, "E5.3.10.2", {"start": v(-110, 236.5) * mm, "end": v(-100, 236.5) * mm});
            skLineSegment(sketch, "E5.3.10.3", {"start": v(-110, 246.5) * mm, "end": v(-100, 246.5) * mm});
            skLineSegment(sketch, "E5.3.11.0", {"start": v(-110, 221.5) * mm, "end": v(-110, 231.5) * mm});
            skLineSegment(sketch, "E5.3.11.1", {"start": v(-100, 221.5) * mm, "end": v(-100, 231.5) * mm});
            skLineSegment(sketch, "E5.3.11.2", {"start": v(-110, 221.5) * mm, "end": v(-100, 221.5) * mm});
            skLineSegment(sketch, "E5.3.11.3", {"start": v(-110, 231.5) * mm, "end": v(-100, 231.5) * mm});
            skLineSegment(sketch, "E5.3.12.0", {"start": v(-110, 206.5) * mm, "end": v(-110, 216.5) * mm});
            skLineSegment(sketch, "E5.3.12.1", {"start": v(-100, 206.5) * mm, "end": v(-100, 216.5) * mm});
            skLineSegment(sketch, "E5.3.12.2", {"start": v(-110, 206.5) * mm, "end": v(-100, 206.5) * mm});
            skLineSegment(sketch, "E5.3.12.3", {"start": v(-110, 216.5) * mm, "end": v(-100, 216.5) * mm});
            skLineSegment(sketch, "E5.3.13.0", {"start": v(-110, 191.5) * mm, "end": v(-110, 201.5) * mm});
            skLineSegment(sketch, "E5.3.13.1", {"start": v(-100, 191.5) * mm, "end": v(-100, 201.5) * mm});
            skLineSegment(sketch, "E5.3.13.2", {"start": v(-110, 191.5) * mm, "end": v(-100, 191.5) * mm});
            skLineSegment(sketch, "E5.3.13.3", {"start": v(-110, 201.5) * mm, "end": v(-100, 201.5) * mm});
            skLineSegment(sketch, "E5.3.14.0", {"start": v(-110, 176.5) * mm, "end": v(-110, 186.5) * mm});
            skLineSegment(sketch, "E5.3.14.1", {"start": v(-100, 176.5) * mm, "end": v(-100, 186.5) * mm});
            skLineSegment(sketch, "E5.3.14.2", {"start": v(-110, 176.5) * mm, "end": v(-100, 176.5) * mm});
            skLineSegment(sketch, "E5.3.14.3", {"start": v(-110, 186.5) * mm, "end": v(-100, 186.5) * mm});
            skLineSegment(sketch, "E5.3.15.0", {"start": v(-110, 161.5) * mm, "end": v(-110, 171.5) * mm});
            skLineSegment(sketch, "E5.3.15.1", {"start": v(-100, 161.5) * mm, "end": v(-100, 171.5) * mm});
            skLineSegment(sketch, "E5.3.15.2", {"start": v(-110, 161.5) * mm, "end": v(-100, 161.5) * mm});
            skLineSegment(sketch, "E5.3.15.3", {"start": v(-110, 171.5) * mm, "end": v(-100, 171.5) * mm});
            skLineSegment(sketch, "E5.3.16.0", {"start": v(-110, 146.5) * mm, "end": v(-110, 156.5) * mm});
            skLineSegment(sketch, "E5.3.16.1", {"start": v(-100, 146.5) * mm, "end": v(-100, 156.5) * mm});
            skLineSegment(sketch, "E5.3.16.2", {"start": v(-110, 146.5) * mm, "end": v(-100, 146.5) * mm});
            skLineSegment(sketch, "E5.3.16.3", {"start": v(-110, 156.5) * mm, "end": v(-100, 156.5) * mm});
            skLineSegment(sketch, "E5.3.17.0", {"start": v(-110, 131.5) * mm, "end": v(-110, 141.5) * mm});
            skLineSegment(sketch, "E5.3.17.1", {"start": v(-100, 131.5) * mm, "end": v(-100, 141.5) * mm});
            skLineSegment(sketch, "E5.3.17.2", {"start": v(-110, 131.5) * mm, "end": v(-100, 131.5) * mm});
            skLineSegment(sketch, "E5.3.17.3", {"start": v(-110, 141.5) * mm, "end": v(-100, 141.5) * mm});
            skLineSegment(sketch, "E5.3.18.0", {"start": v(-110, 116.5) * mm, "end": v(-110, 126.5) * mm});
            skLineSegment(sketch, "E5.3.18.1", {"start": v(-100, 116.5) * mm, "end": v(-100, 126.5) * mm});
            skLineSegment(sketch, "E5.3.18.2", {"start": v(-110, 116.5) * mm, "end": v(-100, 116.5) * mm});
            skLineSegment(sketch, "E5.3.18.3", {"start": v(-110, 126.5) * mm, "end": v(-100, 126.5) * mm});
            skLineSegment(sketch, "E5.3.19.0", {"start": v(-110, 101.5) * mm, "end": v(-110, 111.5) * mm});
            skLineSegment(sketch, "E5.3.19.1", {"start": v(-100, 101.5) * mm, "end": v(-100, 111.5) * mm});
            skLineSegment(sketch, "E5.3.19.2", {"start": v(-110, 101.5) * mm, "end": v(-100, 101.5) * mm});
            skLineSegment(sketch, "E5.3.19.3", {"start": v(-110, 111.5) * mm, "end": v(-100, 111.5) * mm});
            skLineSegment(sketch, "E5.3.20.0", {"start": v(-110, 86.5) * mm, "end": v(-110, 96.5) * mm});
            skLineSegment(sketch, "E5.3.20.1", {"start": v(-100, 86.5) * mm, "end": v(-100, 96.5) * mm});
            skLineSegment(sketch, "E5.3.20.2", {"start": v(-110, 86.5) * mm, "end": v(-100, 86.5) * mm});
            skLineSegment(sketch, "E5.3.20.3", {"start": v(-110, 96.5) * mm, "end": v(-100, 96.5) * mm});
            skLineSegment(sketch, "E5.3.21.0", {"start": v(-110, 71.5) * mm, "end": v(-110, 81.5) * mm});
            skLineSegment(sketch, "E5.3.21.1", {"start": v(-100, 71.5) * mm, "end": v(-100, 81.5) * mm});
            skLineSegment(sketch, "E5.3.21.2", {"start": v(-110, 71.5) * mm, "end": v(-100, 71.5) * mm});
            skLineSegment(sketch, "E5.3.21.3", {"start": v(-110, 81.5) * mm, "end": v(-100, 81.5) * mm});
            skLineSegment(sketch, "E5.3.22.0", {"start": v(-110, 56.5) * mm, "end": v(-110, 66.5) * mm});
            skLineSegment(sketch, "E5.3.22.1", {"start": v(-100, 56.5) * mm, "end": v(-100, 66.5) * mm});
            skLineSegment(sketch, "E5.3.22.2", {"start": v(-110, 56.5) * mm, "end": v(-100, 56.5) * mm});
            skLineSegment(sketch, "E5.3.22.3", {"start": v(-110, 66.5) * mm, "end": v(-100, 66.5) * mm});
            skLineSegment(sketch, "E5.3.23.0", {"start": v(-110, 41.5) * mm, "end": v(-110, 51.5) * mm});
            skLineSegment(sketch, "E5.3.23.1", {"start": v(-100, 41.5) * mm, "end": v(-100, 51.5) * mm});
            skLineSegment(sketch, "E5.3.23.2", {"start": v(-110, 41.5) * mm, "end": v(-100, 41.5) * mm});
            skLineSegment(sketch, "E5.3.23.3", {"start": v(-110, 51.5) * mm, "end": v(-100, 51.5) * mm});
            skLineSegment(sketch, "E5.3.24.0", {"start": v(-110, 26.5) * mm, "end": v(-110, 36.5) * mm});
            skLineSegment(sketch, "E5.3.24.1", {"start": v(-100, 26.5) * mm, "end": v(-100, 36.5) * mm});
            skLineSegment(sketch, "E5.3.24.2", {"start": v(-110, 26.5) * mm, "end": v(-100, 26.5) * mm});
            skLineSegment(sketch, "E5.3.24.3", {"start": v(-110, 36.5) * mm, "end": v(-100, 36.5) * mm});
            skLineSegment(sketch, "E5.4.0.0", {"start": v(-95, 386.5) * mm, "end": v(-95, 396.5) * mm});
            skLineSegment(sketch, "E5.4.0.1", {"start": v(-85, 386.5) * mm, "end": v(-85, 396.5) * mm});
            skLineSegment(sketch, "E5.4.0.2", {"start": v(-95, 386.5) * mm, "end": v(-85, 386.5) * mm});
            skLineSegment(sketch, "E5.4.0.3", {"start": v(-95, 396.5) * mm, "end": v(-85, 396.5) * mm});
            skLineSegment(sketch, "E5.4.1.0", {"start": v(-95, 371.5) * mm, "end": v(-95, 381.5) * mm});
            skLineSegment(sketch, "E5.4.1.1", {"start": v(-85, 371.5) * mm, "end": v(-85, 381.5) * mm});
            skLineSegment(sketch, "E5.4.1.2", {"start": v(-95, 371.5) * mm, "end": v(-85, 371.5) * mm});
            skLineSegment(sketch, "E5.4.1.3", {"start": v(-95, 381.5) * mm, "end": v(-85, 381.5) * mm});
            skLineSegment(sketch, "E5.4.2.0", {"start": v(-95, 356.5) * mm, "end": v(-95, 366.5) * mm});
            skLineSegment(sketch, "E5.4.2.1", {"start": v(-85, 356.5) * mm, "end": v(-85, 366.5) * mm});
            skLineSegment(sketch, "E5.4.2.2", {"start": v(-95, 356.5) * mm, "end": v(-85, 356.5) * mm});
            skLineSegment(sketch, "E5.4.2.3", {"start": v(-95, 366.5) * mm, "end": v(-85, 366.5) * mm});
            skLineSegment(sketch, "E5.4.3.0", {"start": v(-95, 341.5) * mm, "end": v(-95, 351.5) * mm});
            skLineSegment(sketch, "E5.4.3.1", {"start": v(-85, 341.5) * mm, "end": v(-85, 351.5) * mm});
            skLineSegment(sketch, "E5.4.3.2", {"start": v(-95, 341.5) * mm, "end": v(-85, 341.5) * mm});
            skLineSegment(sketch, "E5.4.3.3", {"start": v(-95, 351.5) * mm, "end": v(-85, 351.5) * mm});
            skLineSegment(sketch, "E5.4.4.0", {"start": v(-95, 326.5) * mm, "end": v(-95, 336.5) * mm});
            skLineSegment(sketch, "E5.4.4.1", {"start": v(-85, 326.5) * mm, "end": v(-85, 336.5) * mm});
            skLineSegment(sketch, "E5.4.4.2", {"start": v(-95, 326.5) * mm, "end": v(-85, 326.5) * mm});
            skLineSegment(sketch, "E5.4.4.3", {"start": v(-95, 336.5) * mm, "end": v(-85, 336.5) * mm});
            skLineSegment(sketch, "E5.4.5.0", {"start": v(-95, 311.5) * mm, "end": v(-95, 321.5) * mm});
            skLineSegment(sketch, "E5.4.5.1", {"start": v(-85, 311.5) * mm, "end": v(-85, 321.5) * mm});
            skLineSegment(sketch, "E5.4.5.2", {"start": v(-95, 311.5) * mm, "end": v(-85, 311.5) * mm});
            skLineSegment(sketch, "E5.4.5.3", {"start": v(-95, 321.5) * mm, "end": v(-85, 321.5) * mm});
            skLineSegment(sketch, "E5.4.6.0", {"start": v(-95, 296.5) * mm, "end": v(-95, 306.5) * mm});
            skLineSegment(sketch, "E5.4.6.1", {"start": v(-85, 296.5) * mm, "end": v(-85, 306.5) * mm});
            skLineSegment(sketch, "E5.4.6.2", {"start": v(-95, 296.5) * mm, "end": v(-85, 296.5) * mm});
            skLineSegment(sketch, "E5.4.6.3", {"start": v(-95, 306.5) * mm, "end": v(-85, 306.5) * mm});
            skLineSegment(sketch, "E5.4.7.0", {"start": v(-95, 281.5) * mm, "end": v(-95, 291.5) * mm});
            skLineSegment(sketch, "E5.4.7.1", {"start": v(-85, 281.5) * mm, "end": v(-85, 291.5) * mm});
            skLineSegment(sketch, "E5.4.7.2", {"start": v(-95, 281.5) * mm, "end": v(-85, 281.5) * mm});
            skLineSegment(sketch, "E5.4.7.3", {"start": v(-95, 291.5) * mm, "end": v(-85, 291.5) * mm});
            skLineSegment(sketch, "E5.4.8.0", {"start": v(-95, 266.5) * mm, "end": v(-95, 276.5) * mm});
            skLineSegment(sketch, "E5.4.8.1", {"start": v(-85, 266.5) * mm, "end": v(-85, 276.5) * mm});
            skLineSegment(sketch, "E5.4.8.2", {"start": v(-95, 266.5) * mm, "end": v(-85, 266.5) * mm});
            skLineSegment(sketch, "E5.4.8.3", {"start": v(-95, 276.5) * mm, "end": v(-85, 276.5) * mm});
            skLineSegment(sketch, "E5.4.9.0", {"start": v(-95, 251.5) * mm, "end": v(-95, 261.5) * mm});
            skLineSegment(sketch, "E5.4.9.1", {"start": v(-85, 251.5) * mm, "end": v(-85, 261.5) * mm});
            skLineSegment(sketch, "E5.4.9.2", {"start": v(-95, 251.5) * mm, "end": v(-85, 251.5) * mm});
            skLineSegment(sketch, "E5.4.9.3", {"start": v(-95, 261.5) * mm, "end": v(-85, 261.5) * mm});
            skLineSegment(sketch, "E5.4.10.0", {"start": v(-95, 236.5) * mm, "end": v(-95, 246.5) * mm});
            skLineSegment(sketch, "E5.4.10.1", {"start": v(-85, 236.5) * mm, "end": v(-85, 246.5) * mm});
            skLineSegment(sketch, "E5.4.10.2", {"start": v(-95, 236.5) * mm, "end": v(-85, 236.5) * mm});
            skLineSegment(sketch, "E5.4.10.3", {"start": v(-95, 246.5) * mm, "end": v(-85, 246.5) * mm});
            skLineSegment(sketch, "E5.4.11.0", {"start": v(-95, 221.5) * mm, "end": v(-95, 231.5) * mm});
            skLineSegment(sketch, "E5.4.11.1", {"start": v(-85, 221.5) * mm, "end": v(-85, 231.5) * mm});
            skLineSegment(sketch, "E5.4.11.2", {"start": v(-95, 221.5) * mm, "end": v(-85, 221.5) * mm});
            skLineSegment(sketch, "E5.4.11.3", {"start": v(-95, 231.5) * mm, "end": v(-85, 231.5) * mm});
            skLineSegment(sketch, "E5.4.12.0", {"start": v(-95, 206.5) * mm, "end": v(-95, 216.5) * mm});
            skLineSegment(sketch, "E5.4.12.1", {"start": v(-85, 206.5) * mm, "end": v(-85, 216.5) * mm});
            skLineSegment(sketch, "E5.4.12.2", {"start": v(-95, 206.5) * mm, "end": v(-85, 206.5) * mm});
            skLineSegment(sketch, "E5.4.12.3", {"start": v(-95, 216.5) * mm, "end": v(-85, 216.5) * mm});
            skLineSegment(sketch, "E5.4.13.0", {"start": v(-95, 191.5) * mm, "end": v(-95, 201.5) * mm});
            skLineSegment(sketch, "E5.4.13.1", {"start": v(-85, 191.5) * mm, "end": v(-85, 201.5) * mm});
            skLineSegment(sketch, "E5.4.13.2", {"start": v(-95, 191.5) * mm, "end": v(-85, 191.5) * mm});
            skLineSegment(sketch, "E5.4.13.3", {"start": v(-95, 201.5) * mm, "end": v(-85, 201.5) * mm});
            skLineSegment(sketch, "E5.4.14.0", {"start": v(-95, 176.5) * mm, "end": v(-95, 186.5) * mm});
            skLineSegment(sketch, "E5.4.14.1", {"start": v(-85, 176.5) * mm, "end": v(-85, 186.5) * mm});
            skLineSegment(sketch, "E5.4.14.2", {"start": v(-95, 176.5) * mm, "end": v(-85, 176.5) * mm});
            skLineSegment(sketch, "E5.4.14.3", {"start": v(-95, 186.5) * mm, "end": v(-85, 186.5) * mm});
            skLineSegment(sketch, "E5.4.15.0", {"start": v(-95, 161.5) * mm, "end": v(-95, 171.5) * mm});
            skLineSegment(sketch, "E5.4.15.1", {"start": v(-85, 161.5) * mm, "end": v(-85, 171.5) * mm});
            skLineSegment(sketch, "E5.4.15.2", {"start": v(-95, 161.5) * mm, "end": v(-85, 161.5) * mm});
            skLineSegment(sketch, "E5.4.15.3", {"start": v(-95, 171.5) * mm, "end": v(-85, 171.5) * mm});
            skLineSegment(sketch, "E5.4.16.0", {"start": v(-95, 146.5) * mm, "end": v(-95, 156.5) * mm});
            skLineSegment(sketch, "E5.4.16.1", {"start": v(-85, 146.5) * mm, "end": v(-85, 156.5) * mm});
            skLineSegment(sketch, "E5.4.16.2", {"start": v(-95, 146.5) * mm, "end": v(-85, 146.5) * mm});
            skLineSegment(sketch, "E5.4.16.3", {"start": v(-95, 156.5) * mm, "end": v(-85, 156.5) * mm});
            skLineSegment(sketch, "E5.4.17.0", {"start": v(-95, 131.5) * mm, "end": v(-95, 141.5) * mm});
            skLineSegment(sketch, "E5.4.17.1", {"start": v(-85, 131.5) * mm, "end": v(-85, 141.5) * mm});
            skLineSegment(sketch, "E5.4.17.2", {"start": v(-95, 131.5) * mm, "end": v(-85, 131.5) * mm});
            skLineSegment(sketch, "E5.4.17.3", {"start": v(-95, 141.5) * mm, "end": v(-85, 141.5) * mm});
            skLineSegment(sketch, "E5.4.18.0", {"start": v(-95, 116.5) * mm, "end": v(-95, 126.5) * mm});
            skLineSegment(sketch, "E5.4.18.1", {"start": v(-85, 116.5) * mm, "end": v(-85, 126.5) * mm});
            skLineSegment(sketch, "E5.4.18.2", {"start": v(-95, 116.5) * mm, "end": v(-85, 116.5) * mm});
            skLineSegment(sketch, "E5.4.18.3", {"start": v(-95, 126.5) * mm, "end": v(-85, 126.5) * mm});
            skLineSegment(sketch, "E5.4.19.0", {"start": v(-95, 101.5) * mm, "end": v(-95, 111.5) * mm});
            skLineSegment(sketch, "E5.4.19.1", {"start": v(-85, 101.5) * mm, "end": v(-85, 111.5) * mm});
            skLineSegment(sketch, "E5.4.19.2", {"start": v(-95, 101.5) * mm, "end": v(-85, 101.5) * mm});
            skLineSegment(sketch, "E5.4.19.3", {"start": v(-95, 111.5) * mm, "end": v(-85, 111.5) * mm});
            skLineSegment(sketch, "E5.4.20.0", {"start": v(-95, 86.5) * mm, "end": v(-95, 96.5) * mm});
            skLineSegment(sketch, "E5.4.20.1", {"start": v(-85, 86.5) * mm, "end": v(-85, 96.5) * mm});
            skLineSegment(sketch, "E5.4.20.2", {"start": v(-95, 86.5) * mm, "end": v(-85, 86.5) * mm});
            skLineSegment(sketch, "E5.4.20.3", {"start": v(-95, 96.5) * mm, "end": v(-85, 96.5) * mm});
            skLineSegment(sketch, "E5.4.21.0", {"start": v(-95, 71.5) * mm, "end": v(-95, 81.5) * mm});
            skLineSegment(sketch, "E5.4.21.1", {"start": v(-85, 71.5) * mm, "end": v(-85, 81.5) * mm});
            skLineSegment(sketch, "E5.4.21.2", {"start": v(-95, 71.5) * mm, "end": v(-85, 71.5) * mm});
            skLineSegment(sketch, "E5.4.21.3", {"start": v(-95, 81.5) * mm, "end": v(-85, 81.5) * mm});
            skLineSegment(sketch, "E5.4.22.0", {"start": v(-95, 56.5) * mm, "end": v(-95, 66.5) * mm});
            skLineSegment(sketch, "E5.4.22.1", {"start": v(-85, 56.5) * mm, "end": v(-85, 66.5) * mm});
            skLineSegment(sketch, "E5.4.22.2", {"start": v(-95, 56.5) * mm, "end": v(-85, 56.5) * mm});
            skLineSegment(sketch, "E5.4.22.3", {"start": v(-95, 66.5) * mm, "end": v(-85, 66.5) * mm});
            skLineSegment(sketch, "E5.4.23.0", {"start": v(-95, 41.5) * mm, "end": v(-95, 51.5) * mm});
            skLineSegment(sketch, "E5.4.23.1", {"start": v(-85, 41.5) * mm, "end": v(-85, 51.5) * mm});
            skLineSegment(sketch, "E5.4.23.2", {"start": v(-95, 41.5) * mm, "end": v(-85, 41.5) * mm});
            skLineSegment(sketch, "E5.4.23.3", {"start": v(-95, 51.5) * mm, "end": v(-85, 51.5) * mm});
            skLineSegment(sketch, "E5.4.24.0", {"start": v(-95, 26.5) * mm, "end": v(-95, 36.5) * mm});
            skLineSegment(sketch, "E5.4.24.1", {"start": v(-85, 26.5) * mm, "end": v(-85, 36.5) * mm});
            skLineSegment(sketch, "E5.4.24.2", {"start": v(-95, 26.5) * mm, "end": v(-85, 26.5) * mm});
            skLineSegment(sketch, "E5.4.24.3", {"start": v(-95, 36.5) * mm, "end": v(-85, 36.5) * mm});
            skLineSegment(sketch, "E5.5.0.0", {"start": v(-80, 386.5) * mm, "end": v(-80, 396.5) * mm});
            skLineSegment(sketch, "E5.5.0.1", {"start": v(-70, 386.5) * mm, "end": v(-70, 396.5) * mm});
            skLineSegment(sketch, "E5.5.0.2", {"start": v(-80, 386.5) * mm, "end": v(-70, 386.5) * mm});
            skLineSegment(sketch, "E5.5.0.3", {"start": v(-80, 396.5) * mm, "end": v(-70, 396.5) * mm});
            skLineSegment(sketch, "E5.5.1.0", {"start": v(-80, 371.5) * mm, "end": v(-80, 381.5) * mm});
            skLineSegment(sketch, "E5.5.1.1", {"start": v(-70, 371.5) * mm, "end": v(-70, 381.5) * mm});
            skLineSegment(sketch, "E5.5.1.2", {"start": v(-80, 371.5) * mm, "end": v(-70, 371.5) * mm});
            skLineSegment(sketch, "E5.5.1.3", {"start": v(-80, 381.5) * mm, "end": v(-70, 381.5) * mm});
            skLineSegment(sketch, "E5.5.2.0", {"start": v(-80, 356.5) * mm, "end": v(-80, 366.5) * mm});
            skLineSegment(sketch, "E5.5.2.1", {"start": v(-70, 356.5) * mm, "end": v(-70, 366.5) * mm});
            skLineSegment(sketch, "E5.5.2.2", {"start": v(-80, 356.5) * mm, "end": v(-70, 356.5) * mm});
            skLineSegment(sketch, "E5.5.2.3", {"start": v(-80, 366.5) * mm, "end": v(-70, 366.5) * mm});
            skLineSegment(sketch, "E5.5.3.0", {"start": v(-80, 341.5) * mm, "end": v(-80, 351.5) * mm});
            skLineSegment(sketch, "E5.5.3.1", {"start": v(-70, 341.5) * mm, "end": v(-70, 351.5) * mm});
            skLineSegment(sketch, "E5.5.3.2", {"start": v(-80, 341.5) * mm, "end": v(-70, 341.5) * mm});
            skLineSegment(sketch, "E5.5.3.3", {"start": v(-80, 351.5) * mm, "end": v(-70, 351.5) * mm});
            skLineSegment(sketch, "E5.5.4.0", {"start": v(-80, 326.5) * mm, "end": v(-80, 336.5) * mm});
            skLineSegment(sketch, "E5.5.4.1", {"start": v(-70, 326.5) * mm, "end": v(-70, 336.5) * mm});
            skLineSegment(sketch, "E5.5.4.2", {"start": v(-80, 326.5) * mm, "end": v(-70, 326.5) * mm});
            skLineSegment(sketch, "E5.5.4.3", {"start": v(-80, 336.5) * mm, "end": v(-70, 336.5) * mm});
            skLineSegment(sketch, "E5.5.5.0", {"start": v(-80, 311.5) * mm, "end": v(-80, 321.5) * mm});
            skLineSegment(sketch, "E5.5.5.1", {"start": v(-70, 311.5) * mm, "end": v(-70, 321.5) * mm});
            skLineSegment(sketch, "E5.5.5.2", {"start": v(-80, 311.5) * mm, "end": v(-70, 311.5) * mm});
            skLineSegment(sketch, "E5.5.5.3", {"start": v(-80, 321.5) * mm, "end": v(-70, 321.5) * mm});
            skLineSegment(sketch, "E5.5.6.0", {"start": v(-80, 296.5) * mm, "end": v(-80, 306.5) * mm});
            skLineSegment(sketch, "E5.5.6.1", {"start": v(-70, 296.5) * mm, "end": v(-70, 306.5) * mm});
            skLineSegment(sketch, "E5.5.6.2", {"start": v(-80, 296.5) * mm, "end": v(-70, 296.5) * mm});
            skLineSegment(sketch, "E5.5.6.3", {"start": v(-80, 306.5) * mm, "end": v(-70, 306.5) * mm});
            skLineSegment(sketch, "E5.5.7.0", {"start": v(-80, 281.5) * mm, "end": v(-80, 291.5) * mm});
            skLineSegment(sketch, "E5.5.7.1", {"start": v(-70, 281.5) * mm, "end": v(-70, 291.5) * mm});
            skLineSegment(sketch, "E5.5.7.2", {"start": v(-80, 281.5) * mm, "end": v(-70, 281.5) * mm});
            skLineSegment(sketch, "E5.5.7.3", {"start": v(-80, 291.5) * mm, "end": v(-70, 291.5) * mm});
            skLineSegment(sketch, "E5.5.8.0", {"start": v(-80, 266.5) * mm, "end": v(-80, 276.5) * mm});
            skLineSegment(sketch, "E5.5.8.1", {"start": v(-70, 266.5) * mm, "end": v(-70, 276.5) * mm});
            skLineSegment(sketch, "E5.5.8.2", {"start": v(-80, 266.5) * mm, "end": v(-70, 266.5) * mm});
            skLineSegment(sketch, "E5.5.8.3", {"start": v(-80, 276.5) * mm, "end": v(-70, 276.5) * mm});
            skLineSegment(sketch, "E5.5.9.0", {"start": v(-80, 251.5) * mm, "end": v(-80, 261.5) * mm});
            skLineSegment(sketch, "E5.5.9.1", {"start": v(-70, 251.5) * mm, "end": v(-70, 261.5) * mm});
            skLineSegment(sketch, "E5.5.9.2", {"start": v(-80, 251.5) * mm, "end": v(-70, 251.5) * mm});
            skLineSegment(sketch, "E5.5.9.3", {"start": v(-80, 261.5) * mm, "end": v(-70, 261.5) * mm});
            skLineSegment(sketch, "E5.5.10.0", {"start": v(-80, 236.5) * mm, "end": v(-80, 246.5) * mm});
            skLineSegment(sketch, "E5.5.10.1", {"start": v(-70, 236.5) * mm, "end": v(-70, 246.5) * mm});
            skLineSegment(sketch, "E5.5.10.2", {"start": v(-80, 236.5) * mm, "end": v(-70, 236.5) * mm});
            skLineSegment(sketch, "E5.5.10.3", {"start": v(-80, 246.5) * mm, "end": v(-70, 246.5) * mm});
            skLineSegment(sketch, "E5.5.11.0", {"start": v(-80, 221.5) * mm, "end": v(-80, 231.5) * mm});
            skLineSegment(sketch, "E5.5.11.1", {"start": v(-70, 221.5) * mm, "end": v(-70, 231.5) * mm});
            skLineSegment(sketch, "E5.5.11.2", {"start": v(-80, 221.5) * mm, "end": v(-70, 221.5) * mm});
            skLineSegment(sketch, "E5.5.11.3", {"start": v(-80, 231.5) * mm, "end": v(-70, 231.5) * mm});
            skLineSegment(sketch, "E5.5.12.0", {"start": v(-80, 206.5) * mm, "end": v(-80, 216.5) * mm});
            skLineSegment(sketch, "E5.5.12.1", {"start": v(-70, 206.5) * mm, "end": v(-70, 216.5) * mm});
            skLineSegment(sketch, "E5.5.12.2", {"start": v(-80, 206.5) * mm, "end": v(-70, 206.5) * mm});
            skLineSegment(sketch, "E5.5.12.3", {"start": v(-80, 216.5) * mm, "end": v(-70, 216.5) * mm});
            skLineSegment(sketch, "E5.5.13.0", {"start": v(-80, 191.5) * mm, "end": v(-80, 201.5) * mm});
            skLineSegment(sketch, "E5.5.13.1", {"start": v(-70, 191.5) * mm, "end": v(-70, 201.5) * mm});
            skLineSegment(sketch, "E5.5.13.2", {"start": v(-80, 191.5) * mm, "end": v(-70, 191.5) * mm});
            skLineSegment(sketch, "E5.5.13.3", {"start": v(-80, 201.5) * mm, "end": v(-70, 201.5) * mm});
            skLineSegment(sketch, "E5.5.14.0", {"start": v(-80, 176.5) * mm, "end": v(-80, 186.5) * mm});
            skLineSegment(sketch, "E5.5.14.1", {"start": v(-70, 176.5) * mm, "end": v(-70, 186.5) * mm});
            skLineSegment(sketch, "E5.5.14.2", {"start": v(-80, 176.5) * mm, "end": v(-70, 176.5) * mm});
            skLineSegment(sketch, "E5.5.14.3", {"start": v(-80, 186.5) * mm, "end": v(-70, 186.5) * mm});
            skLineSegment(sketch, "E5.5.15.0", {"start": v(-80, 161.5) * mm, "end": v(-80, 171.5) * mm});
            skLineSegment(sketch, "E5.5.15.1", {"start": v(-70, 161.5) * mm, "end": v(-70, 171.5) * mm});
            skLineSegment(sketch, "E5.5.15.2", {"start": v(-80, 161.5) * mm, "end": v(-70, 161.5) * mm});
            skLineSegment(sketch, "E5.5.15.3", {"start": v(-80, 171.5) * mm, "end": v(-70, 171.5) * mm});
            skLineSegment(sketch, "E5.5.16.0", {"start": v(-80, 146.5) * mm, "end": v(-80, 156.5) * mm});
            skLineSegment(sketch, "E5.5.16.1", {"start": v(-70, 146.5) * mm, "end": v(-70, 156.5) * mm});
            skLineSegment(sketch, "E5.5.16.2", {"start": v(-80, 146.5) * mm, "end": v(-70, 146.5) * mm});
            skLineSegment(sketch, "E5.5.16.3", {"start": v(-80, 156.5) * mm, "end": v(-70, 156.5) * mm});
            skLineSegment(sketch, "E5.5.17.0", {"start": v(-80, 131.5) * mm, "end": v(-80, 141.5) * mm});
            skLineSegment(sketch, "E5.5.17.1", {"start": v(-70, 131.5) * mm, "end": v(-70, 141.5) * mm});
            skLineSegment(sketch, "E5.5.17.2", {"start": v(-80, 131.5) * mm, "end": v(-70, 131.5) * mm});
            skLineSegment(sketch, "E5.5.17.3", {"start": v(-80, 141.5) * mm, "end": v(-70, 141.5) * mm});
            skLineSegment(sketch, "E5.5.18.0", {"start": v(-80, 116.5) * mm, "end": v(-80, 126.5) * mm});
            skLineSegment(sketch, "E5.5.18.1", {"start": v(-70, 116.5) * mm, "end": v(-70, 126.5) * mm});
            skLineSegment(sketch, "E5.5.18.2", {"start": v(-80, 116.5) * mm, "end": v(-70, 116.5) * mm});
            skLineSegment(sketch, "E5.5.18.3", {"start": v(-80, 126.5) * mm, "end": v(-70, 126.5) * mm});
            skLineSegment(sketch, "E5.5.19.0", {"start": v(-80, 101.5) * mm, "end": v(-80, 111.5) * mm});
            skLineSegment(sketch, "E5.5.19.1", {"start": v(-70, 101.5) * mm, "end": v(-70, 111.5) * mm});
            skLineSegment(sketch, "E5.5.19.2", {"start": v(-80, 101.5) * mm, "end": v(-70, 101.5) * mm});
            skLineSegment(sketch, "E5.5.19.3", {"start": v(-80, 111.5) * mm, "end": v(-70, 111.5) * mm});
            skLineSegment(sketch, "E5.5.20.0", {"start": v(-80, 86.5) * mm, "end": v(-80, 96.5) * mm});
            skLineSegment(sketch, "E5.5.20.1", {"start": v(-70, 86.5) * mm, "end": v(-70, 96.5) * mm});
            skLineSegment(sketch, "E5.5.20.2", {"start": v(-80, 86.5) * mm, "end": v(-70, 86.5) * mm});
            skLineSegment(sketch, "E5.5.20.3", {"start": v(-80, 96.5) * mm, "end": v(-70, 96.5) * mm});
            skLineSegment(sketch, "E5.5.21.0", {"start": v(-80, 71.5) * mm, "end": v(-80, 81.5) * mm});
            skLineSegment(sketch, "E5.5.21.1", {"start": v(-70, 71.5) * mm, "end": v(-70, 81.5) * mm});
            skLineSegment(sketch, "E5.5.21.2", {"start": v(-80, 71.5) * mm, "end": v(-70, 71.5) * mm});
            skLineSegment(sketch, "E5.5.21.3", {"start": v(-80, 81.5) * mm, "end": v(-70, 81.5) * mm});
            skLineSegment(sketch, "E5.5.22.0", {"start": v(-80, 56.5) * mm, "end": v(-80, 66.5) * mm});
            skLineSegment(sketch, "E5.5.22.1", {"start": v(-70, 56.5) * mm, "end": v(-70, 66.5) * mm});
            skLineSegment(sketch, "E5.5.22.2", {"start": v(-80, 56.5) * mm, "end": v(-70, 56.5) * mm});
            skLineSegment(sketch, "E5.5.22.3", {"start": v(-80, 66.5) * mm, "end": v(-70, 66.5) * mm});
            skLineSegment(sketch, "E5.5.23.0", {"start": v(-80, 41.5) * mm, "end": v(-80, 51.5) * mm});
            skLineSegment(sketch, "E5.5.23.1", {"start": v(-70, 41.5) * mm, "end": v(-70, 51.5) * mm});
            skLineSegment(sketch, "E5.5.23.2", {"start": v(-80, 41.5) * mm, "end": v(-70, 41.5) * mm});
            skLineSegment(sketch, "E5.5.23.3", {"start": v(-80, 51.5) * mm, "end": v(-70, 51.5) * mm});
            skLineSegment(sketch, "E5.5.24.0", {"start": v(-80, 26.5) * mm, "end": v(-80, 36.5) * mm});
            skLineSegment(sketch, "E5.5.24.1", {"start": v(-70, 26.5) * mm, "end": v(-70, 36.5) * mm});
            skLineSegment(sketch, "E5.5.24.2", {"start": v(-80, 26.5) * mm, "end": v(-70, 26.5) * mm});
            skLineSegment(sketch, "E5.5.24.3", {"start": v(-80, 36.5) * mm, "end": v(-70, 36.5) * mm});
            skLineSegment(sketch, "E5.6.0.0", {"start": v(-65, 386.5) * mm, "end": v(-65, 396.5) * mm});
            skLineSegment(sketch, "E5.6.0.1", {"start": v(-55, 386.5) * mm, "end": v(-55, 396.5) * mm});
            skLineSegment(sketch, "E5.6.0.2", {"start": v(-65, 386.5) * mm, "end": v(-55, 386.5) * mm});
            skLineSegment(sketch, "E5.6.0.3", {"start": v(-65, 396.5) * mm, "end": v(-55, 396.5) * mm});
            skLineSegment(sketch, "E5.6.1.0", {"start": v(-65, 371.5) * mm, "end": v(-65, 381.5) * mm});
            skLineSegment(sketch, "E5.6.1.1", {"start": v(-55, 371.5) * mm, "end": v(-55, 381.5) * mm});
            skLineSegment(sketch, "E5.6.1.2", {"start": v(-65, 371.5) * mm, "end": v(-55, 371.5) * mm});
            skLineSegment(sketch, "E5.6.1.3", {"start": v(-65, 381.5) * mm, "end": v(-55, 381.5) * mm});
            skLineSegment(sketch, "E5.6.2.0", {"start": v(-65, 356.5) * mm, "end": v(-65, 366.5) * mm});
            skLineSegment(sketch, "E5.6.2.1", {"start": v(-55, 356.5) * mm, "end": v(-55, 366.5) * mm});
            skLineSegment(sketch, "E5.6.2.2", {"start": v(-65, 356.5) * mm, "end": v(-55, 356.5) * mm});
            skLineSegment(sketch, "E5.6.2.3", {"start": v(-65, 366.5) * mm, "end": v(-55, 366.5) * mm});
            skLineSegment(sketch, "E5.6.3.0", {"start": v(-65, 341.5) * mm, "end": v(-65, 351.5) * mm});
            skLineSegment(sketch, "E5.6.3.1", {"start": v(-55, 341.5) * mm, "end": v(-55, 351.5) * mm});
            skLineSegment(sketch, "E5.6.3.2", {"start": v(-65, 341.5) * mm, "end": v(-55, 341.5) * mm});
            skLineSegment(sketch, "E5.6.3.3", {"start": v(-65, 351.5) * mm, "end": v(-55, 351.5) * mm});
            skLineSegment(sketch, "E5.6.4.0", {"start": v(-65, 326.5) * mm, "end": v(-65, 336.5) * mm});
            skLineSegment(sketch, "E5.6.4.1", {"start": v(-55, 326.5) * mm, "end": v(-55, 336.5) * mm});
            skLineSegment(sketch, "E5.6.4.2", {"start": v(-65, 326.5) * mm, "end": v(-55, 326.5) * mm});
            skLineSegment(sketch, "E5.6.4.3", {"start": v(-65, 336.5) * mm, "end": v(-55, 336.5) * mm});
            skLineSegment(sketch, "E5.6.5.0", {"start": v(-65, 311.5) * mm, "end": v(-65, 321.5) * mm});
            skLineSegment(sketch, "E5.6.5.1", {"start": v(-55, 311.5) * mm, "end": v(-55, 321.5) * mm});
            skLineSegment(sketch, "E5.6.5.2", {"start": v(-65, 311.5) * mm, "end": v(-55, 311.5) * mm});
            skLineSegment(sketch, "E5.6.5.3", {"start": v(-65, 321.5) * mm, "end": v(-55, 321.5) * mm});
            skLineSegment(sketch, "E5.6.6.0", {"start": v(-65, 296.5) * mm, "end": v(-65, 306.5) * mm});
            skLineSegment(sketch, "E5.6.6.1", {"start": v(-55, 296.5) * mm, "end": v(-55, 306.5) * mm});
            skLineSegment(sketch, "E5.6.6.2", {"start": v(-65, 296.5) * mm, "end": v(-55, 296.5) * mm});
            skLineSegment(sketch, "E5.6.6.3", {"start": v(-65, 306.5) * mm, "end": v(-55, 306.5) * mm});
            skLineSegment(sketch, "E5.6.7.0", {"start": v(-65, 281.5) * mm, "end": v(-65, 291.5) * mm});
            skLineSegment(sketch, "E5.6.7.1", {"start": v(-55, 281.5) * mm, "end": v(-55, 291.5) * mm});
            skLineSegment(sketch, "E5.6.7.2", {"start": v(-65, 281.5) * mm, "end": v(-55, 281.5) * mm});
            skLineSegment(sketch, "E5.6.7.3", {"start": v(-65, 291.5) * mm, "end": v(-55, 291.5) * mm});
            skLineSegment(sketch, "E5.6.8.0", {"start": v(-65, 266.5) * mm, "end": v(-65, 276.5) * mm});
            skLineSegment(sketch, "E5.6.8.1", {"start": v(-55, 266.5) * mm, "end": v(-55, 276.5) * mm});
            skLineSegment(sketch, "E5.6.8.2", {"start": v(-65, 266.5) * mm, "end": v(-55, 266.5) * mm});
            skLineSegment(sketch, "E5.6.8.3", {"start": v(-65, 276.5) * mm, "end": v(-55, 276.5) * mm});
            skLineSegment(sketch, "E5.6.9.0", {"start": v(-65, 251.5) * mm, "end": v(-65, 261.5) * mm});
            skLineSegment(sketch, "E5.6.9.1", {"start": v(-55, 251.5) * mm, "end": v(-55, 261.5) * mm});
            skLineSegment(sketch, "E5.6.9.2", {"start": v(-65, 251.5) * mm, "end": v(-55, 251.5) * mm});
            skLineSegment(sketch, "E5.6.9.3", {"start": v(-65, 261.5) * mm, "end": v(-55, 261.5) * mm});
            skLineSegment(sketch, "E5.6.10.0", {"start": v(-65, 236.5) * mm, "end": v(-65, 246.5) * mm});
            skLineSegment(sketch, "E5.6.10.1", {"start": v(-55, 236.5) * mm, "end": v(-55, 246.5) * mm});
            skLineSegment(sketch, "E5.6.10.2", {"start": v(-65, 236.5) * mm, "end": v(-55, 236.5) * mm});
            skLineSegment(sketch, "E5.6.10.3", {"start": v(-65, 246.5) * mm, "end": v(-55, 246.5) * mm});
            skLineSegment(sketch, "E5.6.11.0", {"start": v(-65, 221.5) * mm, "end": v(-65, 231.5) * mm});
            skLineSegment(sketch, "E5.6.11.1", {"start": v(-55, 221.5) * mm, "end": v(-55, 231.5) * mm});
            skLineSegment(sketch, "E5.6.11.2", {"start": v(-65, 221.5) * mm, "end": v(-55, 221.5) * mm});
            skLineSegment(sketch, "E5.6.11.3", {"start": v(-65, 231.5) * mm, "end": v(-55, 231.5) * mm});
            skLineSegment(sketch, "E5.6.12.0", {"start": v(-65, 206.5) * mm, "end": v(-65, 216.5) * mm});
            skLineSegment(sketch, "E5.6.12.1", {"start": v(-55, 206.5) * mm, "end": v(-55, 216.5) * mm});
            skLineSegment(sketch, "E5.6.12.2", {"start": v(-65, 206.5) * mm, "end": v(-55, 206.5) * mm});
            skLineSegment(sketch, "E5.6.12.3", {"start": v(-65, 216.5) * mm, "end": v(-55, 216.5) * mm});
            skLineSegment(sketch, "E5.6.13.0", {"start": v(-65, 191.5) * mm, "end": v(-65, 201.5) * mm});
            skLineSegment(sketch, "E5.6.13.1", {"start": v(-55, 191.5) * mm, "end": v(-55, 201.5) * mm});
            skLineSegment(sketch, "E5.6.13.2", {"start": v(-65, 191.5) * mm, "end": v(-55, 191.5) * mm});
            skLineSegment(sketch, "E5.6.13.3", {"start": v(-65, 201.5) * mm, "end": v(-55, 201.5) * mm});
            skLineSegment(sketch, "E5.6.14.0", {"start": v(-65, 176.5) * mm, "end": v(-65, 186.5) * mm});
            skLineSegment(sketch, "E5.6.14.1", {"start": v(-55, 176.5) * mm, "end": v(-55, 186.5) * mm});
            skLineSegment(sketch, "E5.6.14.2", {"start": v(-65, 176.5) * mm, "end": v(-55, 176.5) * mm});
            skLineSegment(sketch, "E5.6.14.3", {"start": v(-65, 186.5) * mm, "end": v(-55, 186.5) * mm});
            skLineSegment(sketch, "E5.6.15.0", {"start": v(-65, 161.5) * mm, "end": v(-65, 171.5) * mm});
            skLineSegment(sketch, "E5.6.15.1", {"start": v(-55, 161.5) * mm, "end": v(-55, 171.5) * mm});
            skLineSegment(sketch, "E5.6.15.2", {"start": v(-65, 161.5) * mm, "end": v(-55, 161.5) * mm});
            skLineSegment(sketch, "E5.6.15.3", {"start": v(-65, 171.5) * mm, "end": v(-55, 171.5) * mm});
            skLineSegment(sketch, "E5.6.16.0", {"start": v(-65, 146.5) * mm, "end": v(-65, 156.5) * mm});
            skLineSegment(sketch, "E5.6.16.1", {"start": v(-55, 146.5) * mm, "end": v(-55, 156.5) * mm});
            skLineSegment(sketch, "E5.6.16.2", {"start": v(-65, 146.5) * mm, "end": v(-55, 146.5) * mm});
            skLineSegment(sketch, "E5.6.16.3", {"start": v(-65, 156.5) * mm, "end": v(-55, 156.5) * mm});
            skLineSegment(sketch, "E5.6.17.0", {"start": v(-65, 131.5) * mm, "end": v(-65, 141.5) * mm});
            skLineSegment(sketch, "E5.6.17.1", {"start": v(-55, 131.5) * mm, "end": v(-55, 141.5) * mm});
            skLineSegment(sketch, "E5.6.17.2", {"start": v(-65, 131.5) * mm, "end": v(-55, 131.5) * mm});
            skLineSegment(sketch, "E5.6.17.3", {"start": v(-65, 141.5) * mm, "end": v(-55, 141.5) * mm});
            skLineSegment(sketch, "E5.6.18.0", {"start": v(-65, 116.5) * mm, "end": v(-65, 126.5) * mm});
            skLineSegment(sketch, "E5.6.18.1", {"start": v(-55, 116.5) * mm, "end": v(-55, 126.5) * mm});
            skLineSegment(sketch, "E5.6.18.2", {"start": v(-65, 116.5) * mm, "end": v(-55, 116.5) * mm});
            skLineSegment(sketch, "E5.6.18.3", {"start": v(-65, 126.5) * mm, "end": v(-55, 126.5) * mm});
            skLineSegment(sketch, "E5.6.19.0", {"start": v(-65, 101.5) * mm, "end": v(-65, 111.5) * mm});
            skLineSegment(sketch, "E5.6.19.1", {"start": v(-55, 101.5) * mm, "end": v(-55, 111.5) * mm});
            skLineSegment(sketch, "E5.6.19.2", {"start": v(-65, 101.5) * mm, "end": v(-55, 101.5) * mm});
            skLineSegment(sketch, "E5.6.19.3", {"start": v(-65, 111.5) * mm, "end": v(-55, 111.5) * mm});
            skLineSegment(sketch, "E5.6.20.0", {"start": v(-65, 86.5) * mm, "end": v(-65, 96.5) * mm});
            skLineSegment(sketch, "E5.6.20.1", {"start": v(-55, 86.5) * mm, "end": v(-55, 96.5) * mm});
            skLineSegment(sketch, "E5.6.20.2", {"start": v(-65, 86.5) * mm, "end": v(-55, 86.5) * mm});
            skLineSegment(sketch, "E5.6.20.3", {"start": v(-65, 96.5) * mm, "end": v(-55, 96.5) * mm});
            skLineSegment(sketch, "E5.6.21.0", {"start": v(-65, 71.5) * mm, "end": v(-65, 81.5) * mm});
            skLineSegment(sketch, "E5.6.21.1", {"start": v(-55, 71.5) * mm, "end": v(-55, 81.5) * mm});
            skLineSegment(sketch, "E5.6.21.2", {"start": v(-65, 71.5) * mm, "end": v(-55, 71.5) * mm});
            skLineSegment(sketch, "E5.6.21.3", {"start": v(-65, 81.5) * mm, "end": v(-55, 81.5) * mm});
            skLineSegment(sketch, "E5.6.22.0", {"start": v(-65, 56.5) * mm, "end": v(-65, 66.5) * mm});
            skLineSegment(sketch, "E5.6.22.1", {"start": v(-55, 56.5) * mm, "end": v(-55, 66.5) * mm});
            skLineSegment(sketch, "E5.6.22.2", {"start": v(-65, 56.5) * mm, "end": v(-55, 56.5) * mm});
            skLineSegment(sketch, "E5.6.22.3", {"start": v(-65, 66.5) * mm, "end": v(-55, 66.5) * mm});
            skLineSegment(sketch, "E5.6.23.0", {"start": v(-65, 41.5) * mm, "end": v(-65, 51.5) * mm});
            skLineSegment(sketch, "E5.6.23.1", {"start": v(-55, 41.5) * mm, "end": v(-55, 51.5) * mm});
            skLineSegment(sketch, "E5.6.23.2", {"start": v(-65, 41.5) * mm, "end": v(-55, 41.5) * mm});
            skLineSegment(sketch, "E5.6.23.3", {"start": v(-65, 51.5) * mm, "end": v(-55, 51.5) * mm});
            skLineSegment(sketch, "E5.6.24.0", {"start": v(-65, 26.5) * mm, "end": v(-65, 36.5) * mm});
            skLineSegment(sketch, "E5.6.24.1", {"start": v(-55, 26.5) * mm, "end": v(-55, 36.5) * mm});
            skLineSegment(sketch, "E5.6.24.2", {"start": v(-65, 26.5) * mm, "end": v(-55, 26.5) * mm});
            skLineSegment(sketch, "E5.6.24.3", {"start": v(-65, 36.5) * mm, "end": v(-55, 36.5) * mm});
            skLineSegment(sketch, "E5.7.0.0", {"start": v(-50, 386.5) * mm, "end": v(-50, 396.5) * mm});
            skLineSegment(sketch, "E5.7.0.1", {"start": v(-40, 386.5) * mm, "end": v(-40, 396.5) * mm});
            skLineSegment(sketch, "E5.7.0.2", {"start": v(-50, 386.5) * mm, "end": v(-40, 386.5) * mm});
            skLineSegment(sketch, "E5.7.0.3", {"start": v(-50, 396.5) * mm, "end": v(-40, 396.5) * mm});
            skLineSegment(sketch, "E5.7.1.0", {"start": v(-50, 371.5) * mm, "end": v(-50, 381.5) * mm});
            skLineSegment(sketch, "E5.7.1.1", {"start": v(-40, 371.5) * mm, "end": v(-40, 381.5) * mm});
            skLineSegment(sketch, "E5.7.1.2", {"start": v(-50, 371.5) * mm, "end": v(-40, 371.5) * mm});
            skLineSegment(sketch, "E5.7.1.3", {"start": v(-50, 381.5) * mm, "end": v(-40, 381.5) * mm});
            skLineSegment(sketch, "E5.7.2.0", {"start": v(-50, 356.5) * mm, "end": v(-50, 366.5) * mm});
            skLineSegment(sketch, "E5.7.2.1", {"start": v(-40, 356.5) * mm, "end": v(-40, 366.5) * mm});
            skLineSegment(sketch, "E5.7.2.2", {"start": v(-50, 356.5) * mm, "end": v(-40, 356.5) * mm});
            skLineSegment(sketch, "E5.7.2.3", {"start": v(-50, 366.5) * mm, "end": v(-40, 366.5) * mm});
            skLineSegment(sketch, "E5.7.3.0", {"start": v(-50, 341.5) * mm, "end": v(-50, 351.5) * mm});
            skLineSegment(sketch, "E5.7.3.1", {"start": v(-40, 341.5) * mm, "end": v(-40, 351.5) * mm});
            skLineSegment(sketch, "E5.7.3.2", {"start": v(-50, 341.5) * mm, "end": v(-40, 341.5) * mm});
            skLineSegment(sketch, "E5.7.3.3", {"start": v(-50, 351.5) * mm, "end": v(-40, 351.5) * mm});
            skLineSegment(sketch, "E5.7.4.0", {"start": v(-50, 326.5) * mm, "end": v(-50, 336.5) * mm});
            skLineSegment(sketch, "E5.7.4.1", {"start": v(-40, 326.5) * mm, "end": v(-40, 336.5) * mm});
            skLineSegment(sketch, "E5.7.4.2", {"start": v(-50, 326.5) * mm, "end": v(-40, 326.5) * mm});
            skLineSegment(sketch, "E5.7.4.3", {"start": v(-50, 336.5) * mm, "end": v(-40, 336.5) * mm});
            skLineSegment(sketch, "E5.7.5.0", {"start": v(-50, 311.5) * mm, "end": v(-50, 321.5) * mm});
            skLineSegment(sketch, "E5.7.5.1", {"start": v(-40, 311.5) * mm, "end": v(-40, 321.5) * mm});
            skLineSegment(sketch, "E5.7.5.2", {"start": v(-50, 311.5) * mm, "end": v(-40, 311.5) * mm});
            skLineSegment(sketch, "E5.7.5.3", {"start": v(-50, 321.5) * mm, "end": v(-40, 321.5) * mm});
            skLineSegment(sketch, "E5.7.6.0", {"start": v(-50, 296.5) * mm, "end": v(-50, 306.5) * mm});
            skLineSegment(sketch, "E5.7.6.1", {"start": v(-40, 296.5) * mm, "end": v(-40, 306.5) * mm});
            skLineSegment(sketch, "E5.7.6.2", {"start": v(-50, 296.5) * mm, "end": v(-40, 296.5) * mm});
            skLineSegment(sketch, "E5.7.6.3", {"start": v(-50, 306.5) * mm, "end": v(-40, 306.5) * mm});
            skLineSegment(sketch, "E5.7.7.0", {"start": v(-50, 281.5) * mm, "end": v(-50, 291.5) * mm});
            skLineSegment(sketch, "E5.7.7.1", {"start": v(-40, 281.5) * mm, "end": v(-40, 291.5) * mm});
            skLineSegment(sketch, "E5.7.7.2", {"start": v(-50, 281.5) * mm, "end": v(-40, 281.5) * mm});
            skLineSegment(sketch, "E5.7.7.3", {"start": v(-50, 291.5) * mm, "end": v(-40, 291.5) * mm});
            skLineSegment(sketch, "E5.7.8.0", {"start": v(-50, 266.5) * mm, "end": v(-50, 276.5) * mm});
            skLineSegment(sketch, "E5.7.8.1", {"start": v(-40, 266.5) * mm, "end": v(-40, 276.5) * mm});
            skLineSegment(sketch, "E5.7.8.2", {"start": v(-50, 266.5) * mm, "end": v(-40, 266.5) * mm});
            skLineSegment(sketch, "E5.7.8.3", {"start": v(-50, 276.5) * mm, "end": v(-40, 276.5) * mm});
            skLineSegment(sketch, "E5.7.9.0", {"start": v(-50, 251.5) * mm, "end": v(-50, 261.5) * mm});
            skLineSegment(sketch, "E5.7.9.1", {"start": v(-40, 251.5) * mm, "end": v(-40, 261.5) * mm});
            skLineSegment(sketch, "E5.7.9.2", {"start": v(-50, 251.5) * mm, "end": v(-40, 251.5) * mm});
            skLineSegment(sketch, "E5.7.9.3", {"start": v(-50, 261.5) * mm, "end": v(-40, 261.5) * mm});
            skLineSegment(sketch, "E5.7.10.0", {"start": v(-50, 236.5) * mm, "end": v(-50, 246.5) * mm});
            skLineSegment(sketch, "E5.7.10.1", {"start": v(-40, 236.5) * mm, "end": v(-40, 246.5) * mm});
            skLineSegment(sketch, "E5.7.10.2", {"start": v(-50, 236.5) * mm, "end": v(-40, 236.5) * mm});
            skLineSegment(sketch, "E5.7.10.3", {"start": v(-50, 246.5) * mm, "end": v(-40, 246.5) * mm});
            skLineSegment(sketch, "E5.7.11.0", {"start": v(-50, 221.5) * mm, "end": v(-50, 231.5) * mm});
            skLineSegment(sketch, "E5.7.11.1", {"start": v(-40, 221.5) * mm, "end": v(-40, 231.5) * mm});
            skLineSegment(sketch, "E5.7.11.2", {"start": v(-50, 221.5) * mm, "end": v(-40, 221.5) * mm});
            skLineSegment(sketch, "E5.7.11.3", {"start": v(-50, 231.5) * mm, "end": v(-40, 231.5) * mm});
            skLineSegment(sketch, "E5.7.12.0", {"start": v(-50, 206.5) * mm, "end": v(-50, 216.5) * mm});
            skLineSegment(sketch, "E5.7.12.1", {"start": v(-40, 206.5) * mm, "end": v(-40, 216.5) * mm});
            skLineSegment(sketch, "E5.7.12.2", {"start": v(-50, 206.5) * mm, "end": v(-40, 206.5) * mm});
            skLineSegment(sketch, "E5.7.12.3", {"start": v(-50, 216.5) * mm, "end": v(-40, 216.5) * mm});
            skLineSegment(sketch, "E5.7.13.0", {"start": v(-50, 191.5) * mm, "end": v(-50, 201.5) * mm});
            skLineSegment(sketch, "E5.7.13.1", {"start": v(-40, 191.5) * mm, "end": v(-40, 201.5) * mm});
            skLineSegment(sketch, "E5.7.13.2", {"start": v(-50, 191.5) * mm, "end": v(-40, 191.5) * mm});
            skLineSegment(sketch, "E5.7.13.3", {"start": v(-50, 201.5) * mm, "end": v(-40, 201.5) * mm});
            skLineSegment(sketch, "E5.7.14.0", {"start": v(-50, 176.5) * mm, "end": v(-50, 186.5) * mm});
            skLineSegment(sketch, "E5.7.14.1", {"start": v(-40, 176.5) * mm, "end": v(-40, 186.5) * mm});
            skLineSegment(sketch, "E5.7.14.2", {"start": v(-50, 176.5) * mm, "end": v(-40, 176.5) * mm});
            skLineSegment(sketch, "E5.7.14.3", {"start": v(-50, 186.5) * mm, "end": v(-40, 186.5) * mm});
            skLineSegment(sketch, "E5.7.15.0", {"start": v(-50, 161.5) * mm, "end": v(-50, 171.5) * mm});
            skLineSegment(sketch, "E5.7.15.1", {"start": v(-40, 161.5) * mm, "end": v(-40, 171.5) * mm});
            skLineSegment(sketch, "E5.7.15.2", {"start": v(-50, 161.5) * mm, "end": v(-40, 161.5) * mm});
            skLineSegment(sketch, "E5.7.15.3", {"start": v(-50, 171.5) * mm, "end": v(-40, 171.5) * mm});
            skLineSegment(sketch, "E5.7.16.0", {"start": v(-50, 146.5) * mm, "end": v(-50, 156.5) * mm});
            skLineSegment(sketch, "E5.7.16.1", {"start": v(-40, 146.5) * mm, "end": v(-40, 156.5) * mm});
            skLineSegment(sketch, "E5.7.16.2", {"start": v(-50, 146.5) * mm, "end": v(-40, 146.5) * mm});
            skLineSegment(sketch, "E5.7.16.3", {"start": v(-50, 156.5) * mm, "end": v(-40, 156.5) * mm});
            skLineSegment(sketch, "E5.7.17.0", {"start": v(-50, 131.5) * mm, "end": v(-50, 141.5) * mm});
            skLineSegment(sketch, "E5.7.17.1", {"start": v(-40, 131.5) * mm, "end": v(-40, 141.5) * mm});
            skLineSegment(sketch, "E5.7.17.2", {"start": v(-50, 131.5) * mm, "end": v(-40, 131.5) * mm});
            skLineSegment(sketch, "E5.7.17.3", {"start": v(-50, 141.5) * mm, "end": v(-40, 141.5) * mm});
            skLineSegment(sketch, "E5.7.18.0", {"start": v(-50, 116.5) * mm, "end": v(-50, 126.5) * mm});
            skLineSegment(sketch, "E5.7.18.1", {"start": v(-40, 116.5) * mm, "end": v(-40, 126.5) * mm});
            skLineSegment(sketch, "E5.7.18.2", {"start": v(-50, 116.5) * mm, "end": v(-40, 116.5) * mm});
            skLineSegment(sketch, "E5.7.18.3", {"start": v(-50, 126.5) * mm, "end": v(-40, 126.5) * mm});
            skLineSegment(sketch, "E5.7.19.0", {"start": v(-50, 101.5) * mm, "end": v(-50, 111.5) * mm});
            skLineSegment(sketch, "E5.7.19.1", {"start": v(-40, 101.5) * mm, "end": v(-40, 111.5) * mm});
            skLineSegment(sketch, "E5.7.19.2", {"start": v(-50, 101.5) * mm, "end": v(-40, 101.5) * mm});
            skLineSegment(sketch, "E5.7.19.3", {"start": v(-50, 111.5) * mm, "end": v(-40, 111.5) * mm});
            skLineSegment(sketch, "E5.7.20.0", {"start": v(-50, 86.5) * mm, "end": v(-50, 96.5) * mm});
            skLineSegment(sketch, "E5.7.20.1", {"start": v(-40, 86.5) * mm, "end": v(-40, 96.5) * mm});
            skLineSegment(sketch, "E5.7.20.2", {"start": v(-50, 86.5) * mm, "end": v(-40, 86.5) * mm});
            skLineSegment(sketch, "E5.7.20.3", {"start": v(-50, 96.5) * mm, "end": v(-40, 96.5) * mm});
            skLineSegment(sketch, "E5.7.21.0", {"start": v(-50, 71.5) * mm, "end": v(-50, 81.5) * mm});
            skLineSegment(sketch, "E5.7.21.1", {"start": v(-40, 71.5) * mm, "end": v(-40, 81.5) * mm});
            skLineSegment(sketch, "E5.7.21.2", {"start": v(-50, 71.5) * mm, "end": v(-40, 71.5) * mm});
            skLineSegment(sketch, "E5.7.21.3", {"start": v(-50, 81.5) * mm, "end": v(-40, 81.5) * mm});
            skLineSegment(sketch, "E5.7.22.0", {"start": v(-50, 56.5) * mm, "end": v(-50, 66.5) * mm});
            skLineSegment(sketch, "E5.7.22.1", {"start": v(-40, 56.5) * mm, "end": v(-40, 66.5) * mm});
            skLineSegment(sketch, "E5.7.22.2", {"start": v(-50, 56.5) * mm, "end": v(-40, 56.5) * mm});
            skLineSegment(sketch, "E5.7.22.3", {"start": v(-50, 66.5) * mm, "end": v(-40, 66.5) * mm});
            skLineSegment(sketch, "E5.7.23.0", {"start": v(-50, 41.5) * mm, "end": v(-50, 51.5) * mm});
            skLineSegment(sketch, "E5.7.23.1", {"start": v(-40, 41.5) * mm, "end": v(-40, 51.5) * mm});
            skLineSegment(sketch, "E5.7.23.2", {"start": v(-50, 41.5) * mm, "end": v(-40, 41.5) * mm});
            skLineSegment(sketch, "E5.7.23.3", {"start": v(-50, 51.5) * mm, "end": v(-40, 51.5) * mm});
            skLineSegment(sketch, "E5.7.24.0", {"start": v(-50, 26.5) * mm, "end": v(-50, 36.5) * mm});
            skLineSegment(sketch, "E5.7.24.1", {"start": v(-40, 26.5) * mm, "end": v(-40, 36.5) * mm});
            skLineSegment(sketch, "E5.7.24.2", {"start": v(-50, 26.5) * mm, "end": v(-40, 26.5) * mm});
            skLineSegment(sketch, "E5.7.24.3", {"start": v(-50, 36.5) * mm, "end": v(-40, 36.5) * mm});
            skLineSegment(sketch, "E5.8.0.0", {"start": v(-35, 386.5) * mm, "end": v(-35, 396.5) * mm});
            skLineSegment(sketch, "E5.8.0.1", {"start": v(-25, 386.5) * mm, "end": v(-25, 396.5) * mm});
            skLineSegment(sketch, "E5.8.0.2", {"start": v(-35, 386.5) * mm, "end": v(-25, 386.5) * mm});
            skLineSegment(sketch, "E5.8.0.3", {"start": v(-35, 396.5) * mm, "end": v(-25, 396.5) * mm});
            skLineSegment(sketch, "E5.8.1.0", {"start": v(-35, 371.5) * mm, "end": v(-35, 381.5) * mm});
            skLineSegment(sketch, "E5.8.1.1", {"start": v(-25, 371.5) * mm, "end": v(-25, 381.5) * mm});
            skLineSegment(sketch, "E5.8.1.2", {"start": v(-35, 371.5) * mm, "end": v(-25, 371.5) * mm});
            skLineSegment(sketch, "E5.8.1.3", {"start": v(-35, 381.5) * mm, "end": v(-25, 381.5) * mm});
            skLineSegment(sketch, "E5.8.2.0", {"start": v(-35, 356.5) * mm, "end": v(-35, 366.5) * mm});
            skLineSegment(sketch, "E5.8.2.1", {"start": v(-25, 356.5) * mm, "end": v(-25, 366.5) * mm});
            skLineSegment(sketch, "E5.8.2.2", {"start": v(-35, 356.5) * mm, "end": v(-25, 356.5) * mm});
            skLineSegment(sketch, "E5.8.2.3", {"start": v(-35, 366.5) * mm, "end": v(-25, 366.5) * mm});
            skLineSegment(sketch, "E5.8.3.0", {"start": v(-35, 341.5) * mm, "end": v(-35, 351.5) * mm});
            skLineSegment(sketch, "E5.8.3.1", {"start": v(-25, 341.5) * mm, "end": v(-25, 351.5) * mm});
            skLineSegment(sketch, "E5.8.3.2", {"start": v(-35, 341.5) * mm, "end": v(-25, 341.5) * mm});
            skLineSegment(sketch, "E5.8.3.3", {"start": v(-35, 351.5) * mm, "end": v(-25, 351.5) * mm});
            skLineSegment(sketch, "E5.8.4.0", {"start": v(-35, 326.5) * mm, "end": v(-35, 336.5) * mm});
            skLineSegment(sketch, "E5.8.4.1", {"start": v(-25, 326.5) * mm, "end": v(-25, 336.5) * mm});
            skLineSegment(sketch, "E5.8.4.2", {"start": v(-35, 326.5) * mm, "end": v(-25, 326.5) * mm});
            skLineSegment(sketch, "E5.8.4.3", {"start": v(-35, 336.5) * mm, "end": v(-25, 336.5) * mm});
            skLineSegment(sketch, "E5.8.5.0", {"start": v(-35, 311.5) * mm, "end": v(-35, 321.5) * mm});
            skLineSegment(sketch, "E5.8.5.1", {"start": v(-25, 311.5) * mm, "end": v(-25, 321.5) * mm});
            skLineSegment(sketch, "E5.8.5.2", {"start": v(-35, 311.5) * mm, "end": v(-25, 311.5) * mm});
            skLineSegment(sketch, "E5.8.5.3", {"start": v(-35, 321.5) * mm, "end": v(-25, 321.5) * mm});
            skLineSegment(sketch, "E5.8.6.0", {"start": v(-35, 296.5) * mm, "end": v(-35, 306.5) * mm});
            skLineSegment(sketch, "E5.8.6.1", {"start": v(-25, 296.5) * mm, "end": v(-25, 306.5) * mm});
            skLineSegment(sketch, "E5.8.6.2", {"start": v(-35, 296.5) * mm, "end": v(-25, 296.5) * mm});
            skLineSegment(sketch, "E5.8.6.3", {"start": v(-35, 306.5) * mm, "end": v(-25, 306.5) * mm});
            skLineSegment(sketch, "E5.8.7.0", {"start": v(-35, 281.5) * mm, "end": v(-35, 291.5) * mm});
            skLineSegment(sketch, "E5.8.7.1", {"start": v(-25, 281.5) * mm, "end": v(-25, 291.5) * mm});
            skLineSegment(sketch, "E5.8.7.2", {"start": v(-35, 281.5) * mm, "end": v(-25, 281.5) * mm});
            skLineSegment(sketch, "E5.8.7.3", {"start": v(-35, 291.5) * mm, "end": v(-25, 291.5) * mm});
            skLineSegment(sketch, "E5.8.8.0", {"start": v(-35, 266.5) * mm, "end": v(-35, 276.5) * mm});
            skLineSegment(sketch, "E5.8.8.1", {"start": v(-25, 266.5) * mm, "end": v(-25, 276.5) * mm});
            skLineSegment(sketch, "E5.8.8.2", {"start": v(-35, 266.5) * mm, "end": v(-25, 266.5) * mm});
            skLineSegment(sketch, "E5.8.8.3", {"start": v(-35, 276.5) * mm, "end": v(-25, 276.5) * mm});
            skLineSegment(sketch, "E5.8.9.0", {"start": v(-35, 251.5) * mm, "end": v(-35, 261.5) * mm});
            skLineSegment(sketch, "E5.8.9.1", {"start": v(-25, 251.5) * mm, "end": v(-25, 261.5) * mm});
            skLineSegment(sketch, "E5.8.9.2", {"start": v(-35, 251.5) * mm, "end": v(-25, 251.5) * mm});
            skLineSegment(sketch, "E5.8.9.3", {"start": v(-35, 261.5) * mm, "end": v(-25, 261.5) * mm});
            skLineSegment(sketch, "E5.8.10.0", {"start": v(-35, 236.5) * mm, "end": v(-35, 246.5) * mm});
            skLineSegment(sketch, "E5.8.10.1", {"start": v(-25, 236.5) * mm, "end": v(-25, 246.5) * mm});
            skLineSegment(sketch, "E5.8.10.2", {"start": v(-35, 236.5) * mm, "end": v(-25, 236.5) * mm});
            skLineSegment(sketch, "E5.8.10.3", {"start": v(-35, 246.5) * mm, "end": v(-25, 246.5) * mm});
            skLineSegment(sketch, "E5.8.11.0", {"start": v(-35, 221.5) * mm, "end": v(-35, 231.5) * mm});
            skLineSegment(sketch, "E5.8.11.1", {"start": v(-25, 221.5) * mm, "end": v(-25, 231.5) * mm});
            skLineSegment(sketch, "E5.8.11.2", {"start": v(-35, 221.5) * mm, "end": v(-25, 221.5) * mm});
            skLineSegment(sketch, "E5.8.11.3", {"start": v(-35, 231.5) * mm, "end": v(-25, 231.5) * mm});
            skLineSegment(sketch, "E5.8.12.0", {"start": v(-35, 206.5) * mm, "end": v(-35, 216.5) * mm});
            skLineSegment(sketch, "E5.8.12.1", {"start": v(-25, 206.5) * mm, "end": v(-25, 216.5) * mm});
            skLineSegment(sketch, "E5.8.12.2", {"start": v(-35, 206.5) * mm, "end": v(-25, 206.5) * mm});
            skLineSegment(sketch, "E5.8.12.3", {"start": v(-35, 216.5) * mm, "end": v(-25, 216.5) * mm});
            skLineSegment(sketch, "E5.8.13.0", {"start": v(-35, 191.5) * mm, "end": v(-35, 201.5) * mm});
            skLineSegment(sketch, "E5.8.13.1", {"start": v(-25, 191.5) * mm, "end": v(-25, 201.5) * mm});
            skLineSegment(sketch, "E5.8.13.2", {"start": v(-35, 191.5) * mm, "end": v(-25, 191.5) * mm});
            skLineSegment(sketch, "E5.8.13.3", {"start": v(-35, 201.5) * mm, "end": v(-25, 201.5) * mm});
            skLineSegment(sketch, "E5.8.14.0", {"start": v(-35, 176.5) * mm, "end": v(-35, 186.5) * mm});
            skLineSegment(sketch, "E5.8.14.1", {"start": v(-25, 176.5) * mm, "end": v(-25, 186.5) * mm});
            skLineSegment(sketch, "E5.8.14.2", {"start": v(-35, 176.5) * mm, "end": v(-25, 176.5) * mm});
            skLineSegment(sketch, "E5.8.14.3", {"start": v(-35, 186.5) * mm, "end": v(-25, 186.5) * mm});
            skLineSegment(sketch, "E5.8.15.0", {"start": v(-35, 161.5) * mm, "end": v(-35, 171.5) * mm});
            skLineSegment(sketch, "E5.8.15.1", {"start": v(-25, 161.5) * mm, "end": v(-25, 171.5) * mm});
            skLineSegment(sketch, "E5.8.15.2", {"start": v(-35, 161.5) * mm, "end": v(-25, 161.5) * mm});
            skLineSegment(sketch, "E5.8.15.3", {"start": v(-35, 171.5) * mm, "end": v(-25, 171.5) * mm});
            skLineSegment(sketch, "E5.8.16.0", {"start": v(-35, 146.5) * mm, "end": v(-35, 156.5) * mm});
            skLineSegment(sketch, "E5.8.16.1", {"start": v(-25, 146.5) * mm, "end": v(-25, 156.5) * mm});
            skLineSegment(sketch, "E5.8.16.2", {"start": v(-35, 146.5) * mm, "end": v(-25, 146.5) * mm});
            skLineSegment(sketch, "E5.8.16.3", {"start": v(-35, 156.5) * mm, "end": v(-25, 156.5) * mm});
            skLineSegment(sketch, "E5.8.17.0", {"start": v(-35, 131.5) * mm, "end": v(-35, 141.5) * mm});
            skLineSegment(sketch, "E5.8.17.1", {"start": v(-25, 131.5) * mm, "end": v(-25, 141.5) * mm});
            skLineSegment(sketch, "E5.8.17.2", {"start": v(-35, 131.5) * mm, "end": v(-25, 131.5) * mm});
            skLineSegment(sketch, "E5.8.17.3", {"start": v(-35, 141.5) * mm, "end": v(-25, 141.5) * mm});
            skLineSegment(sketch, "E5.8.18.0", {"start": v(-35, 116.5) * mm, "end": v(-35, 126.5) * mm});
            skLineSegment(sketch, "E5.8.18.1", {"start": v(-25, 116.5) * mm, "end": v(-25, 126.5) * mm});
            skLineSegment(sketch, "E5.8.18.2", {"start": v(-35, 116.5) * mm, "end": v(-25, 116.5) * mm});
            skLineSegment(sketch, "E5.8.18.3", {"start": v(-35, 126.5) * mm, "end": v(-25, 126.5) * mm});
            skLineSegment(sketch, "E5.8.19.0", {"start": v(-35, 101.5) * mm, "end": v(-35, 111.5) * mm});
            skLineSegment(sketch, "E5.8.19.1", {"start": v(-25, 101.5) * mm, "end": v(-25, 111.5) * mm});
            skLineSegment(sketch, "E5.8.19.2", {"start": v(-35, 101.5) * mm, "end": v(-25, 101.5) * mm});
            skLineSegment(sketch, "E5.8.19.3", {"start": v(-35, 111.5) * mm, "end": v(-25, 111.5) * mm});
            skLineSegment(sketch, "E5.8.20.0", {"start": v(-35, 86.5) * mm, "end": v(-35, 96.5) * mm});
            skLineSegment(sketch, "E5.8.20.1", {"start": v(-25, 86.5) * mm, "end": v(-25, 96.5) * mm});
            skLineSegment(sketch, "E5.8.20.2", {"start": v(-35, 86.5) * mm, "end": v(-25, 86.5) * mm});
            skLineSegment(sketch, "E5.8.20.3", {"start": v(-35, 96.5) * mm, "end": v(-25, 96.5) * mm});
            skLineSegment(sketch, "E5.8.21.0", {"start": v(-35, 71.5) * mm, "end": v(-35, 81.5) * mm});
            skLineSegment(sketch, "E5.8.21.1", {"start": v(-25, 71.5) * mm, "end": v(-25, 81.5) * mm});
            skLineSegment(sketch, "E5.8.21.2", {"start": v(-35, 71.5) * mm, "end": v(-25, 71.5) * mm});
            skLineSegment(sketch, "E5.8.21.3", {"start": v(-35, 81.5) * mm, "end": v(-25, 81.5) * mm});
            skLineSegment(sketch, "E5.8.22.0", {"start": v(-35, 56.5) * mm, "end": v(-35, 66.5) * mm});
            skLineSegment(sketch, "E5.8.22.1", {"start": v(-25, 56.5) * mm, "end": v(-25, 66.5) * mm});
            skLineSegment(sketch, "E5.8.22.2", {"start": v(-35, 56.5) * mm, "end": v(-25, 56.5) * mm});
            skLineSegment(sketch, "E5.8.22.3", {"start": v(-35, 66.5) * mm, "end": v(-25, 66.5) * mm});
            skLineSegment(sketch, "E5.8.23.0", {"start": v(-35, 41.5) * mm, "end": v(-35, 51.5) * mm});
            skLineSegment(sketch, "E5.8.23.1", {"start": v(-25, 41.5) * mm, "end": v(-25, 51.5) * mm});
            skLineSegment(sketch, "E5.8.23.2", {"start": v(-35, 41.5) * mm, "end": v(-25, 41.5) * mm});
            skLineSegment(sketch, "E5.8.23.3", {"start": v(-35, 51.5) * mm, "end": v(-25, 51.5) * mm});
            skLineSegment(sketch, "E5.8.24.0", {"start": v(-35, 26.5) * mm, "end": v(-35, 36.5) * mm});
            skLineSegment(sketch, "E5.8.24.1", {"start": v(-25, 26.5) * mm, "end": v(-25, 36.5) * mm});
            skLineSegment(sketch, "E5.8.24.2", {"start": v(-35, 26.5) * mm, "end": v(-25, 26.5) * mm});
            skLineSegment(sketch, "E5.8.24.3", {"start": v(-35, 36.5) * mm, "end": v(-25, 36.5) * mm});
            skLineSegment(sketch, "E5.direction1", {"start": v(-157, 385) * mm, "end": v(-142, 385) * mm, "construction": true});
            skLineSegment(sketch, "E5.direction2", {"start": v(-157, 385) * mm, "end": v(-157, 370) * mm, "construction": true});
            skPoint(sketch, "E6.visualSharp", {"position": v(-145, 396.5) * mm});
            skArc(sketch, "E6.filletArc", {"start": v(-145, 395) * mm, "mid": v(-145.44, 396.06) * mm, "end": v(-146.5, 396.5) * mm});
            skPoint(sketch, "E7.visualSharp", {"position": v(-155, 396.5) * mm});
            skArc(sketch, "E7.filletArc", {"start": v(-153.5, 396.5) * mm, "mid": v(-154.56, 396.06) * mm, "end": v(-155, 395) * mm});
            skSolve(sketch);
        }
        {
            var Q0;
            Q0=makeQuery(id+"F0.imprint","IMPRINT",FACE,{"disambiguationData":[TD([[makeQuery(id+"F0.imprint","IMPRINT",EDGE,{"derivedFrom":sQuery(id+"F0.wireOp",EDGE,"E0.bottom")}),-1.0]])]});
            extrude(context, id + "F1", {"entities" : qUnion([Q0]), "depth" : 25 * mm});
        }
        {
            var Q0;
            Q0=qSketchRegion(id+"F0",true);
            extrude(context, id + "F2", {"entities" : qUnion([Q0]), "operationType" : NewBodyOperationType.ADD, "depth" : 25 * mm});
        }
    });
